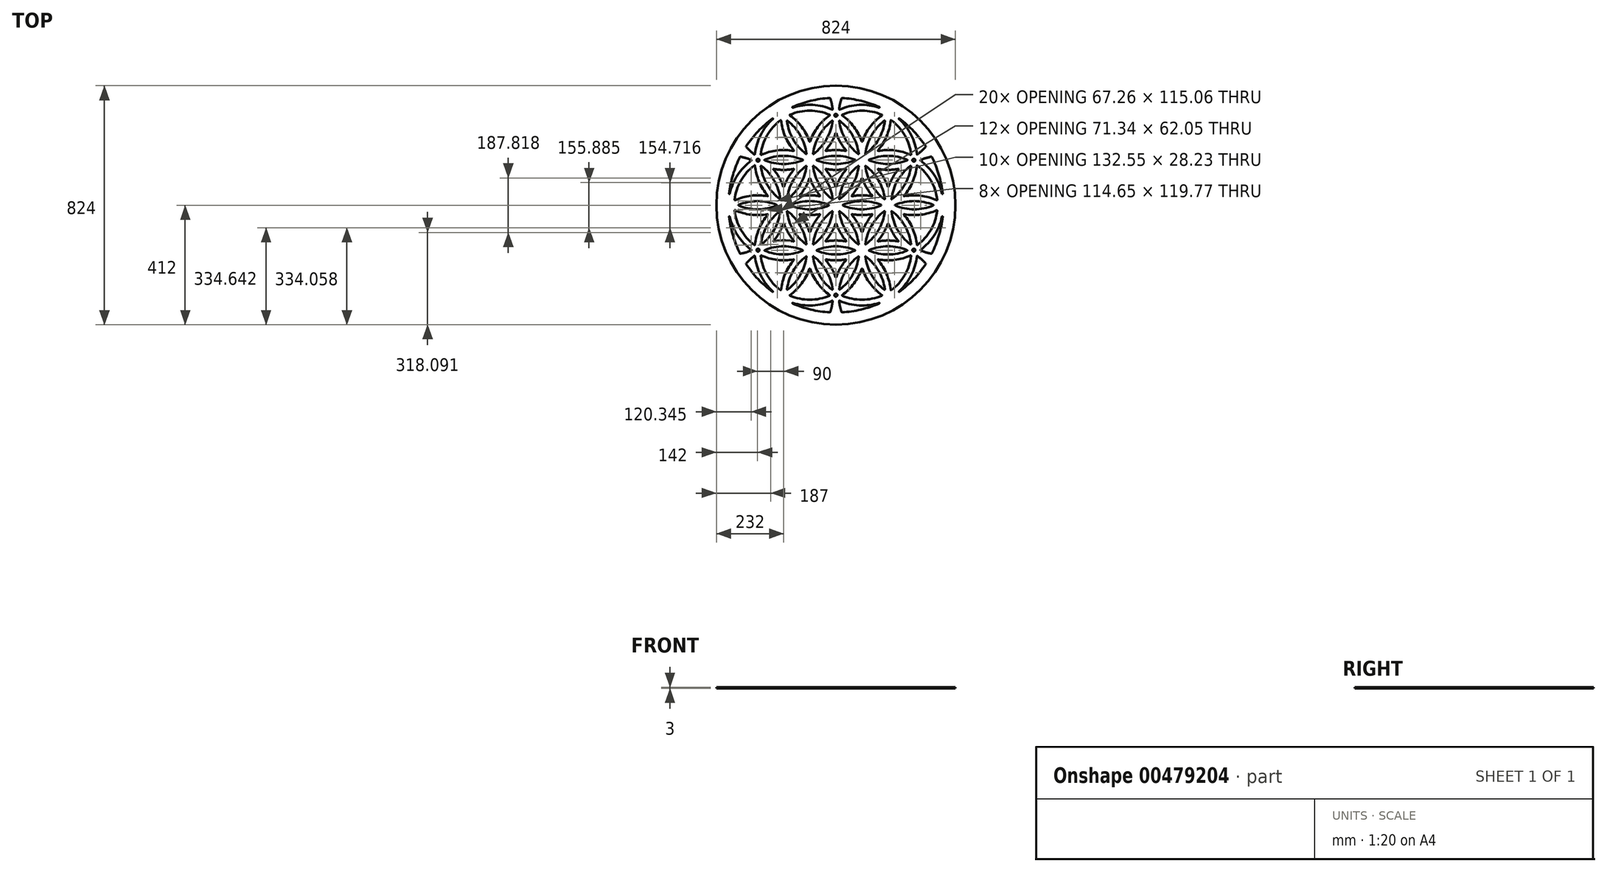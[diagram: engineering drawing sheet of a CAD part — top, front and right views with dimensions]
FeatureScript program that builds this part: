
annotation { "Feature Type Name" : "Feature", "Feature Type Description" : "" }
export const myFeature = defineFeature(function(context is Context, id is Id, definition is map)
    precondition{}
    {
        {
            var Q0;
            Q0=qCreatedBy(makeId("Top.planeOp"),FACE);
            var sketch = newSketch(context, id + "F0", { "sketchPlane" : qUnion([Q0])});
            skArc(sketch, "E0", {"start": v(-280.58, 137.05) * mm, "mid": v(-327.22, 85) * mm, "end": v(-348.98, 18.58) * mm});
            skArc(sketch, "E1", {"start": v(-291.41, 153.9) * mm, "mid": v(-339.34, 103.5) * mm, "end": v(-365.91, 39.2) * mm});
            skArc(sketch, "E2", {"start": v(-190.58, 292.94) * mm, "mid": v(-237.22, 240.88) * mm, "end": v(-258.98, 174.46) * mm});
            skArc(sketch, "E3", {"start": v(-21.41, 309.8) * mm, "mid": v(-62.1, 269.75) * mm, "end": v(-89.06, 219.43) * mm});
            skArc(sketch, "E4", {"start": v(257.58, 173.44) * mm, "mid": v(202.56, 188.66) * mm, "end": v(145.5, 186.84) * mm});
            skArc(sketch, "E5", {"start": v(179.06, 63.55) * mm, "mid": v(164.54, 95) * mm, "end": v(144.56, 123.3) * mm});
            skArc(sketch, "E6", {"start": v(-234.56, -32.6) * mm, "mid": v(-264.66, -81.1) * mm, "end": v(-279, -136.35) * mm});
            skArc(sketch, "E7", {"start": v(-192.97, -20.62) * mm, "mid": v(-237.22, -70.88) * mm, "end": v(-258.63, -134.35) * mm});
            skArc(sketch, "E8", {"start": v(155.66, 0.92) * mm, "mid": v(90, 14.12) * mm, "end": v(24.34, 0.92) * mm});
            skCircle(sketch, "E9", {"center": v(0, 0) * mm, "radius": 412 * mm});
            skArc(sketch, "E10", {"start": v(329.26, 167.2) * mm, "mid": v(310.1, 162.5) * mm, "end": v(291.6, 155.63) * mm});
            skArc(sketch, "E11", {"start": v(309.43, -201.55) * mm, "mid": v(295.78, -187.3) * mm, "end": v(280.58, -174.72) * mm});
            skArc(sketch, "E12", {"start": v(-214.5, 124.93) * mm, "mid": v(-180, 121.77) * mm, "end": v(-145.5, 124.93) * mm});
            skArc(sketch, "E13", {"start": v(-309.43, 201.55) * mm, "mid": v(-295.78, 187.3) * mm, "end": v(-280.58, 174.72) * mm});
            skArc(sketch, "E14", {"start": v(19.83, 368.75) * mm, "mid": v(14.3, 349.8) * mm, "end": v(11.02, 330.35) * mm});
            skArc(sketch, "E15", {"start": v(-20.83, 369.41) * mm, "mid": v(-86.68, 359.7) * mm, "end": v(-149.71, 338.36) * mm});
            skArc(sketch, "E16.trimOffspring", {"start": v(-329.26, -167.2) * mm, "mid": v(-310.1, -162.5) * mm, "end": v(-291.6, -155.63) * mm});
            skArc(sketch, "E17.trimOffspring", {"start": v(-19.83, -368.75) * mm, "mid": v(-14.3, -349.8) * mm, "end": v(-11.02, -330.35) * mm});
            skArc(sketch, "E18.trimOffspring", {"start": v(-189, 292.24) * mm, "mid": v(-174.66, 236.98) * mm, "end": v(-144.56, 188.47) * mm});
            skArc(sketch, "E19.trimOffspring", {"start": v(-12.42, 329.32) * mm, "mid": v(-80.04, 345.62) * mm, "end": v(-149, 336.5) * mm});
            skArc(sketch, "E20.trimOffspring", {"start": v(-11.02, 330.35) * mm, "mid": v(-14.3, 349.8) * mm, "end": v(-19.83, 368.75) * mm});
            skArc(sketch, "E21.trimOffspring", {"start": v(0.94, 248.22) * mm, "mid": v(15.46, 216.77) * mm, "end": v(35.44, 188.47) * mm});
            skArc(sketch, "E22.trimOffspring", {"start": v(-21.6, 311.52) * mm, "mid": v(-90, 325.88) * mm, "end": v(-158.4, 311.52) * mm});
            skArc(sketch, "E23.trimOffspring", {"start": v(11.37, 290.23) * mm, "mid": v(32.78, 226.77) * mm, "end": v(77.03, 176.5) * mm});
            skArc(sketch, "E24.trimOffspring", {"start": v(-12.97, 291.15) * mm, "mid": v(-57.22, 240.88) * mm, "end": v(-78.63, 177.42) * mm});
            skArc(sketch, "E25.trimOffspring", {"start": v(158.59, 309.8) * mm, "mid": v(117.9, 269.75) * mm, "end": v(90.94, 219.43) * mm});
            skArc(sketch, "E26.trimOffspring", {"start": v(167.03, 291.15) * mm, "mid": v(122.78, 240.88) * mm, "end": v(101.37, 177.42) * mm});
            skArc(sketch, "E27.trimOffspring", {"start": v(158.4, 311.52) * mm, "mid": v(90, 325.88) * mm, "end": v(21.6, 311.52) * mm});
            skArc(sketch, "E28.trimOffspring", {"start": v(-279, 136.35) * mm, "mid": v(-264.66, 81.1) * mm, "end": v(-234.56, 32.6) * mm});
            skArc(sketch, "E29.trimOffspring", {"start": v(-291.6, 155.63) * mm, "mid": v(-310.1, 162.5) * mm, "end": v(-329.26, 167.2) * mm});
            skArc(sketch, "E30.trimOffspring", {"start": v(-258.63, 134.35) * mm, "mid": v(-237.22, 70.88) * mm, "end": v(-192.97, 20.62) * mm});
            skArc(sketch, "E31.trimOffspring", {"start": v(-245.66, 154.96) * mm, "mid": v(-180, 141.77) * mm, "end": v(-114.34, 154.96) * mm});
            skArc(sketch, "E32.trimOffspring", {"start": v(280.58, 174.72) * mm, "mid": v(295.78, 187.3) * mm, "end": v(309.43, 201.55) * mm});
            skArc(sketch, "E33.trimOffspring", {"start": v(279, 175.42) * mm, "mid": v(259.3, 242.13) * mm, "end": v(216.91, 297.28) * mm});
            skArc(sketch, "E34.trimOffspring", {"start": v(257.03, 135.27) * mm, "mid": v(212.78, 85) * mm, "end": v(191.37, 21.54) * mm});
            skArc(sketch, "E35.trimOffspring", {"start": v(245.66, 156.8) * mm, "mid": v(180, 170) * mm, "end": v(114.34, 156.8) * mm});
            skArc(sketch, "E36.trimOffspring", {"start": v(215.44, 123.3) * mm, "mid": v(195.46, 95) * mm, "end": v(180.94, 63.55) * mm});
            skArc(sketch, "E37.trimOffspring", {"start": v(258.98, 174.46) * mm, "mid": v(237.22, 240.88) * mm, "end": v(190.58, 292.94) * mm});
            skArc(sketch, "E38.trimOffspring", {"start": v(235.5, -30.96) * mm, "mid": v(292.56, -32.77) * mm, "end": v(347.58, -17.56) * mm});
            skArc(sketch, "E39.trimOffspring", {"start": v(204.34, -0.92) * mm, "mid": v(270, -14.12) * mm, "end": v(335.66, -0.92) * mm});
            skArc(sketch, "E40.trimOffspring", {"start": v(234.56, 32.6) * mm, "mid": v(264.66, 81.1) * mm, "end": v(279, 136.35) * mm});
            skArc(sketch, "E41.trimOffspring", {"start": v(180.94, -63.55) * mm, "mid": v(195.46, -95) * mm, "end": v(215.44, -123.3) * mm});
            skArc(sketch, "E42.trimOffspring", {"start": v(192.97, 20.62) * mm, "mid": v(237.22, 70.88) * mm, "end": v(258.63, 134.35) * mm});
            skArc(sketch, "E43.trimOffspring", {"start": v(124.5, 30.96) * mm, "mid": v(90, 34.12) * mm, "end": v(55.5, 30.96) * mm});
            skArc(sketch, "E44.trimOffspring", {"start": v(125.44, -32.6) * mm, "mid": v(105.46, -60.88) * mm, "end": v(90.94, -92.34) * mm});
            skArc(sketch, "E45.trimOffspring", {"start": v(167.03, -20.62) * mm, "mid": v(122.78, -70.88) * mm, "end": v(101.37, -134.35) * mm});
            skArc(sketch, "E46.trimOffspring", {"start": v(168.63, 21.54) * mm, "mid": v(147.22, 85) * mm, "end": v(102.97, 135.27) * mm});
            skArc(sketch, "E47.trimOffspring", {"start": v(191.37, -21.54) * mm, "mid": v(212.78, -85) * mm, "end": v(257.03, -135.27) * mm});
            skArc(sketch, "E48.trimOffspring", {"start": v(145.5, 124.93) * mm, "mid": v(180, 121.77) * mm, "end": v(214.5, 124.93) * mm});
            skArc(sketch, "E49.trimOffspring", {"start": v(-348.98, -18.58) * mm, "mid": v(-327.22, -85) * mm, "end": v(-280.58, -137.05) * mm});
            skArc(sketch, "E50.trimOffspring", {"start": v(-335.66, -0.92) * mm, "mid": v(-270, -14.12) * mm, "end": v(-204.34, -0.92) * mm});
            skArc(sketch, "E51.trimOffspring", {"start": v(-347.58, -17.56) * mm, "mid": v(-292.56, -32.77) * mm, "end": v(-235.5, -30.96) * mm});
            skArc(sketch, "E52.trimOffspring", {"start": v(-365.91, -39.2) * mm, "mid": v(-339.34, -103.5) * mm, "end": v(-291.41, -153.9) * mm});
            skArc(sketch, "E53.trimOffspring", {"start": v(-145.5, 186.84) * mm, "mid": v(-202.56, 188.66) * mm, "end": v(-257.58, 173.44) * mm});
            skArc(sketch, "E54.trimOffspring", {"start": v(-77.03, 176.5) * mm, "mid": v(-32.78, 226.77) * mm, "end": v(-11.37, 290.23) * mm});
            skArc(sketch, "E55.trimOffspring", {"start": v(-168.63, 290.23) * mm, "mid": v(-147.22, 226.77) * mm, "end": v(-102.97, 176.5) * mm});
            skArc(sketch, "E56.trimOffspring", {"start": v(-34.5, 124.93) * mm, "mid": v(0, 121.77) * mm, "end": v(34.5, 124.93) * mm});
            skArc(sketch, "E57.trimOffspring", {"start": v(-78.63, 134.35) * mm, "mid": v(-57.22, 70.88) * mm, "end": v(-12.97, 20.62) * mm});
            skArc(sketch, "E58.trimOffspring", {"start": v(-89.06, 92.34) * mm, "mid": v(-74.54, 60.88) * mm, "end": v(-54.56, 32.6) * mm});
            skArc(sketch, "E59.trimOffspring", {"start": v(-102.97, 135.27) * mm, "mid": v(-147.22, 85) * mm, "end": v(-168.63, 21.54) * mm});
            skArc(sketch, "E60.trimOffspring", {"start": v(-114.34, 156.8) * mm, "mid": v(-180, 170) * mm, "end": v(-245.66, 156.8) * mm});
            skArc(sketch, "E61.trimOffspring", {"start": v(-144.56, 123.3) * mm, "mid": v(-164.54, 95) * mm, "end": v(-179.06, 63.55) * mm});
            skArc(sketch, "E62.trimOffspring", {"start": v(-180.94, 63.55) * mm, "mid": v(-195.46, 95) * mm, "end": v(-215.44, 123.3) * mm});
            skArc(sketch, "E63.trimOffspring", {"start": v(-35.44, 188.47) * mm, "mid": v(-15.46, 216.77) * mm, "end": v(-0.94, 248.22) * mm});
            skArc(sketch, "E64.trimOffspring", {"start": v(34.5, 186.84) * mm, "mid": v(0, 190) * mm, "end": v(-34.5, 186.84) * mm});
            skArc(sketch, "E65.trimOffspring", {"start": v(-90.94, 219.43) * mm, "mid": v(-117.9, 269.75) * mm, "end": v(-158.59, 309.8) * mm});
            skArc(sketch, "E66.trimOffspring", {"start": v(-101.37, 177.42) * mm, "mid": v(-122.78, 240.88) * mm, "end": v(-167.03, 291.15) * mm});
            skArc(sketch, "E67.trimOffspring", {"start": v(-65.66, 154.96) * mm, "mid": v(0, 141.77) * mm, "end": v(65.66, 154.96) * mm});
            skArc(sketch, "E68.trimOffspring", {"start": v(-216.91, 297.28) * mm, "mid": v(-259.3, 242.13) * mm, "end": v(-279, 175.42) * mm});
            skArc(sketch, "E69.trimOffspring", {"start": v(-218.17, 298.84) * mm, "mid": v(-268.18, 254.92) * mm, "end": v(-309.5, 202.75) * mm});
            skArc(sketch, "E70.trimOffspring", {"start": v(-330.34, 166.67) * mm, "mid": v(-354.85, 104.79) * mm, "end": v(-367.88, 39.52) * mm});
            skArc(sketch, "E71.trimOffspring", {"start": v(149, 336.5) * mm, "mid": v(80.04, 345.62) * mm, "end": v(12.42, 329.32) * mm});
            skArc(sketch, "E72.trimOffspring", {"start": v(149.71, 338.36) * mm, "mid": v(86.68, 359.7) * mm, "end": v(20.83, 369.41) * mm});
            skArc(sketch, "E73.trimOffspring", {"start": v(309.5, 202.75) * mm, "mid": v(268.18, 254.92) * mm, "end": v(218.17, 298.84) * mm});
            skArc(sketch, "E74.trimOffspring", {"start": v(90.94, 92.34) * mm, "mid": v(105.46, 60.88) * mm, "end": v(125.44, 32.6) * mm});
            skArc(sketch, "E75.trimOffspring", {"start": v(35.44, 123.3) * mm, "mid": v(15.46, 95) * mm, "end": v(0.94, 63.55) * mm});
            skArc(sketch, "E76.trimOffspring", {"start": v(89.06, 219.43) * mm, "mid": v(62.1, 269.75) * mm, "end": v(21.41, 309.8) * mm});
            skArc(sketch, "E77.trimOffspring", {"start": v(144.56, 188.47) * mm, "mid": v(174.66, 236.98) * mm, "end": v(189, 292.24) * mm});
            skArc(sketch, "E78.trimOffspring", {"start": v(102.97, 176.5) * mm, "mid": v(147.22, 226.77) * mm, "end": v(168.63, 290.23) * mm});
            skArc(sketch, "E79.trimOffspring", {"start": v(78.63, 177.42) * mm, "mid": v(57.22, 240.88) * mm, "end": v(12.97, 291.15) * mm});
            skArc(sketch, "E80.trimOffspring", {"start": v(114.34, 154.96) * mm, "mid": v(180, 141.77) * mm, "end": v(245.66, 154.96) * mm});
            skArc(sketch, "E81.trimOffspring", {"start": v(101.37, 134.35) * mm, "mid": v(122.78, 70.88) * mm, "end": v(167.03, 20.62) * mm});
            skArc(sketch, "E82.trimOffspring", {"start": v(77.03, 135.27) * mm, "mid": v(32.78, 85) * mm, "end": v(11.37, 21.54) * mm});
            skArc(sketch, "E83.trimOffspring", {"start": v(65.66, 156.8) * mm, "mid": v(0, 170) * mm, "end": v(-65.66, 156.8) * mm});
            skArc(sketch, "E84.trimOffspring", {"start": v(-367.88, -39.52) * mm, "mid": v(-354.85, -104.79) * mm, "end": v(-330.34, -166.67) * mm});
            skArc(sketch, "E85.trimOffspring", {"start": v(-235.5, 30.96) * mm, "mid": v(-292.56, 32.77) * mm, "end": v(-347.58, 17.56) * mm});
            skArc(sketch, "E86.trimOffspring", {"start": v(-124.5, -30.96) * mm, "mid": v(-90, -34.12) * mm, "end": v(-55.5, -30.96) * mm});
            skArc(sketch, "E87.trimOffspring", {"start": v(-179.06, -63.55) * mm, "mid": v(-164.54, -95) * mm, "end": v(-144.56, -123.3) * mm});
            skArc(sketch, "E88.trimOffspring", {"start": v(-125.44, 32.6) * mm, "mid": v(-105.46, 60.88) * mm, "end": v(-90.94, 92.34) * mm});
            skArc(sketch, "E89.trimOffspring", {"start": v(-204.34, 0.92) * mm, "mid": v(-270, 14.12) * mm, "end": v(-335.66, 0.92) * mm});
            skArc(sketch, "E90.trimOffspring", {"start": v(-191.37, 21.54) * mm, "mid": v(-212.78, 85) * mm, "end": v(-257.03, 135.27) * mm});
            skArc(sketch, "E91.trimOffspring", {"start": v(-167.03, 20.62) * mm, "mid": v(-122.78, 70.88) * mm, "end": v(-101.37, 134.35) * mm});
            skArc(sketch, "E92.trimOffspring", {"start": v(-155.66, -0.92) * mm, "mid": v(-90, -14.12) * mm, "end": v(-24.34, -0.92) * mm});
            skArc(sketch, "E93.trimOffspring", {"start": v(-168.63, -21.54) * mm, "mid": v(-147.22, -85) * mm, "end": v(-102.97, -135.27) * mm});
            skArc(sketch, "E94.trimOffspring", {"start": v(335.66, 0.92) * mm, "mid": v(270, 14.12) * mm, "end": v(204.34, 0.92) * mm});
            skArc(sketch, "E95.trimOffspring", {"start": v(347.58, 17.56) * mm, "mid": v(292.56, 32.77) * mm, "end": v(235.5, 30.96) * mm});
            skArc(sketch, "E96.trimOffspring", {"start": v(348.98, 18.58) * mm, "mid": v(327.22, 85) * mm, "end": v(280.58, 137.05) * mm});
            skArc(sketch, "E97.trimOffspring", {"start": v(365.91, 39.2) * mm, "mid": v(339.34, 103.5) * mm, "end": v(291.41, 153.9) * mm});
            skArc(sketch, "E98.trimOffspring", {"start": v(367.88, 39.52) * mm, "mid": v(354.85, 104.79) * mm, "end": v(330.34, 166.67) * mm});
            skArc(sketch, "E99.trimOffspring", {"start": v(-11.37, 21.54) * mm, "mid": v(-32.78, 85) * mm, "end": v(-77.03, 135.27) * mm});
            skArc(sketch, "E100.trimOffspring", {"start": v(-0.94, 63.55) * mm, "mid": v(-15.46, 95) * mm, "end": v(-35.44, 123.3) * mm});
            skArc(sketch, "E101.trimOffspring", {"start": v(12.97, 20.62) * mm, "mid": v(57.22, 70.88) * mm, "end": v(78.63, 134.35) * mm});
            skArc(sketch, "E102.trimOffspring", {"start": v(54.56, 32.6) * mm, "mid": v(74.54, 60.88) * mm, "end": v(89.06, 92.34) * mm});
            skArc(sketch, "E103.trimOffspring", {"start": v(24.34, -0.92) * mm, "mid": v(90, -14.12) * mm, "end": v(155.66, -0.92) * mm});
            skArc(sketch, "E104.trimOffspring", {"start": v(55.5, -30.96) * mm, "mid": v(90, -34.12) * mm, "end": v(124.5, -30.96) * mm});
            skArc(sketch, "E105.trimOffspring", {"start": v(0.94, -63.55) * mm, "mid": v(15.46, -95) * mm, "end": v(35.44, -123.3) * mm});
            skArc(sketch, "E106.trimOffspring", {"start": v(11.37, -21.54) * mm, "mid": v(32.78, -85) * mm, "end": v(77.03, -135.27) * mm});
            skArc(sketch, "E107.trimOffspring", {"start": v(-12.97, -20.62) * mm, "mid": v(-57.22, -70.88) * mm, "end": v(-78.63, -134.35) * mm});
            skArc(sketch, "E108.trimOffspring", {"start": v(-54.56, -32.6) * mm, "mid": v(-74.54, -60.88) * mm, "end": v(-89.06, -92.34) * mm});
            skArc(sketch, "E109.trimOffspring", {"start": v(-24.34, 0.92) * mm, "mid": v(-90, 14.12) * mm, "end": v(-155.66, 0.92) * mm});
            skArc(sketch, "E110.trimOffspring", {"start": v(-55.5, 30.96) * mm, "mid": v(-90, 34.12) * mm, "end": v(-124.5, 30.96) * mm});
            skArc(sketch, "E111.trimOffspring", {"start": v(-309.5, -202.75) * mm, "mid": v(-268.18, -254.92) * mm, "end": v(-218.17, -298.84) * mm});
            skArc(sketch, "E112.trimOffspring", {"start": v(-279, -175.42) * mm, "mid": v(-259.3, -242.13) * mm, "end": v(-216.91, -297.28) * mm});
            skArc(sketch, "E113.trimOffspring", {"start": v(-280.58, -174.72) * mm, "mid": v(-295.78, -187.3) * mm, "end": v(-309.43, -201.55) * mm});
            skArc(sketch, "E114.trimOffspring", {"start": v(-215.44, -123.3) * mm, "mid": v(-195.46, -95) * mm, "end": v(-180.94, -63.55) * mm});
            skArc(sketch, "E115.trimOffspring", {"start": v(-257.03, -135.27) * mm, "mid": v(-212.78, -85) * mm, "end": v(-191.37, -21.54) * mm});
            skArc(sketch, "E116.trimOffspring", {"start": v(-257.58, -173.44) * mm, "mid": v(-202.56, -188.66) * mm, "end": v(-145.5, -186.84) * mm});
            skArc(sketch, "E117.trimOffspring", {"start": v(-258.98, -174.46) * mm, "mid": v(-237.22, -240.88) * mm, "end": v(-190.58, -292.94) * mm});
            skArc(sketch, "E118.trimOffspring", {"start": v(-245.66, -156.8) * mm, "mid": v(-180, -170) * mm, "end": v(-114.34, -156.8) * mm});
            skArc(sketch, "E119.trimOffspring", {"start": v(-167.03, -291.15) * mm, "mid": v(-122.78, -240.88) * mm, "end": v(-101.37, -177.42) * mm});
            skArc(sketch, "E120.trimOffspring", {"start": v(-149, -336.5) * mm, "mid": v(-80.04, -345.62) * mm, "end": v(-12.42, -329.32) * mm});
            skArc(sketch, "E121.trimOffspring", {"start": v(-149.71, -338.36) * mm, "mid": v(-86.68, -359.7) * mm, "end": v(-20.83, -369.41) * mm});
            skArc(sketch, "E122.trimOffspring", {"start": v(-158.59, -309.8) * mm, "mid": v(-117.9, -269.75) * mm, "end": v(-90.94, -219.43) * mm});
            skArc(sketch, "E123.trimOffspring", {"start": v(-158.4, -311.52) * mm, "mid": v(-90, -325.88) * mm, "end": v(-21.6, -311.52) * mm});
            skArc(sketch, "E124.trimOffspring", {"start": v(-114.34, -154.96) * mm, "mid": v(-180, -141.77) * mm, "end": v(-245.66, -154.96) * mm});
            skArc(sketch, "E125.trimOffspring", {"start": v(-145.5, -124.93) * mm, "mid": v(-180, -121.77) * mm, "end": v(-214.5, -124.93) * mm});
            skArc(sketch, "E126.trimOffspring", {"start": v(-101.37, -134.35) * mm, "mid": v(-122.78, -70.88) * mm, "end": v(-167.03, -20.62) * mm});
            skArc(sketch, "E127.trimOffspring", {"start": v(-90.94, -92.34) * mm, "mid": v(-105.46, -60.88) * mm, "end": v(-125.44, -32.6) * mm});
            skArc(sketch, "E128.trimOffspring", {"start": v(-77.03, -135.27) * mm, "mid": v(-32.78, -85) * mm, "end": v(-11.37, -21.54) * mm});
            skArc(sketch, "E129.trimOffspring", {"start": v(-35.44, -123.3) * mm, "mid": v(-15.46, -95) * mm, "end": v(-0.94, -63.55) * mm});
            skArc(sketch, "E130.trimOffspring", {"start": v(-65.66, -156.8) * mm, "mid": v(0, -170) * mm, "end": v(65.66, -156.8) * mm});
            skArc(sketch, "E131.trimOffspring", {"start": v(-34.5, -186.84) * mm, "mid": v(0, -190) * mm, "end": v(34.5, -186.84) * mm});
            skArc(sketch, "E132.trimOffspring", {"start": v(-78.63, -177.42) * mm, "mid": v(-57.22, -240.88) * mm, "end": v(-12.97, -291.15) * mm});
            skArc(sketch, "E133.trimOffspring", {"start": v(-89.06, -219.43) * mm, "mid": v(-62.1, -269.75) * mm, "end": v(-21.41, -309.8) * mm});
            skArc(sketch, "E134.trimOffspring", {"start": v(-102.97, -176.5) * mm, "mid": v(-147.22, -226.77) * mm, "end": v(-168.63, -290.23) * mm});
            skArc(sketch, "E135.trimOffspring", {"start": v(-144.56, -188.47) * mm, "mid": v(-174.66, -236.98) * mm, "end": v(-189, -292.24) * mm});
            skArc(sketch, "E136.trimOffspring", {"start": v(65.66, -154.96) * mm, "mid": v(0, -141.77) * mm, "end": v(-65.66, -154.96) * mm});
            skArc(sketch, "E137.trimOffspring", {"start": v(34.5, -124.93) * mm, "mid": v(0, -121.77) * mm, "end": v(-34.5, -124.93) * mm});
            skArc(sketch, "E138.trimOffspring", {"start": v(78.63, -134.35) * mm, "mid": v(57.22, -70.88) * mm, "end": v(12.97, -20.62) * mm});
            skArc(sketch, "E139.trimOffspring", {"start": v(89.06, -92.34) * mm, "mid": v(74.54, -60.88) * mm, "end": v(54.56, -32.6) * mm});
            skArc(sketch, "E140.trimOffspring", {"start": v(102.97, -135.27) * mm, "mid": v(147.22, -85) * mm, "end": v(168.63, -21.54) * mm});
            skArc(sketch, "E141.trimOffspring", {"start": v(144.56, -123.3) * mm, "mid": v(164.54, -95) * mm, "end": v(179.06, -63.55) * mm});
            skArc(sketch, "E142.trimOffspring", {"start": v(114.34, -156.8) * mm, "mid": v(180, -170) * mm, "end": v(245.66, -156.8) * mm});
            skArc(sketch, "E143.trimOffspring", {"start": v(145.5, -186.84) * mm, "mid": v(202.56, -188.66) * mm, "end": v(257.58, -173.44) * mm});
            skArc(sketch, "E144.trimOffspring", {"start": v(101.37, -177.42) * mm, "mid": v(122.78, -240.88) * mm, "end": v(167.03, -291.15) * mm});
            skArc(sketch, "E145.trimOffspring", {"start": v(90.94, -219.43) * mm, "mid": v(117.9, -269.75) * mm, "end": v(158.59, -309.8) * mm});
            skArc(sketch, "E146.trimOffspring", {"start": v(77.03, -176.5) * mm, "mid": v(32.78, -226.77) * mm, "end": v(11.37, -290.23) * mm});
            skArc(sketch, "E147.trimOffspring", {"start": v(35.44, -188.47) * mm, "mid": v(15.46, -216.77) * mm, "end": v(0.94, -248.22) * mm});
            skArc(sketch, "E148.trimOffspring", {"start": v(214.5, -124.93) * mm, "mid": v(180, -121.77) * mm, "end": v(145.5, -124.93) * mm});
            skArc(sketch, "E149.trimOffspring", {"start": v(280.58, -137.05) * mm, "mid": v(327.22, -85) * mm, "end": v(348.98, -18.58) * mm});
            skArc(sketch, "E150.trimOffspring", {"start": v(279, -136.35) * mm, "mid": v(264.66, -81.1) * mm, "end": v(234.56, -32.6) * mm});
            skArc(sketch, "E151.trimOffspring", {"start": v(258.63, -134.35) * mm, "mid": v(237.22, -70.88) * mm, "end": v(192.97, -20.62) * mm});
            skArc(sketch, "E152.trimOffspring", {"start": v(245.66, -154.96) * mm, "mid": v(180, -141.77) * mm, "end": v(114.34, -154.96) * mm});
            skArc(sketch, "E153.trimOffspring", {"start": v(291.41, -153.9) * mm, "mid": v(339.34, -103.5) * mm, "end": v(365.91, -39.2) * mm});
            skArc(sketch, "E154.trimOffspring", {"start": v(291.6, -155.63) * mm, "mid": v(310.1, -162.5) * mm, "end": v(329.26, -167.2) * mm});
            skArc(sketch, "E155.trimOffspring", {"start": v(330.34, -166.67) * mm, "mid": v(354.85, -104.79) * mm, "end": v(367.88, -39.52) * mm});
            skArc(sketch, "E156.trimOffspring", {"start": v(168.63, -290.23) * mm, "mid": v(147.22, -226.77) * mm, "end": v(102.97, -176.5) * mm});
            skArc(sketch, "E157.trimOffspring", {"start": v(190.58, -292.94) * mm, "mid": v(237.22, -240.88) * mm, "end": v(258.98, -174.46) * mm});
            skArc(sketch, "E158.trimOffspring", {"start": v(189, -292.24) * mm, "mid": v(174.66, -236.98) * mm, "end": v(144.56, -188.47) * mm});
            skArc(sketch, "E159.trimOffspring", {"start": v(218.17, -298.84) * mm, "mid": v(268.18, -254.92) * mm, "end": v(309.5, -202.75) * mm});
            skArc(sketch, "E160.trimOffspring", {"start": v(216.91, -297.28) * mm, "mid": v(259.3, -242.13) * mm, "end": v(279, -175.42) * mm});
            skArc(sketch, "E161.trimOffspring", {"start": v(20.83, -369.41) * mm, "mid": v(86.68, -359.7) * mm, "end": v(149.71, -338.36) * mm});
            skArc(sketch, "E162.trimOffspring", {"start": v(-0.94, -248.22) * mm, "mid": v(-15.46, -216.77) * mm, "end": v(-35.44, -188.47) * mm});
            skArc(sketch, "E163.trimOffspring", {"start": v(12.42, -329.32) * mm, "mid": v(80.04, -345.62) * mm, "end": v(149, -336.5) * mm});
            skArc(sketch, "E164.trimOffspring", {"start": v(21.6, -311.52) * mm, "mid": v(90, -325.88) * mm, "end": v(158.4, -311.52) * mm});
            skArc(sketch, "E165.trimOffspring", {"start": v(21.41, -309.8) * mm, "mid": v(62.1, -269.75) * mm, "end": v(89.06, -219.43) * mm});
            skArc(sketch, "E166.trimOffspring", {"start": v(11.02, -330.35) * mm, "mid": v(14.3, -349.8) * mm, "end": v(19.83, -368.75) * mm});
            skArc(sketch, "E167.trimOffspring", {"start": v(-11.37, -290.23) * mm, "mid": v(-32.78, -226.77) * mm, "end": v(-77.03, -176.5) * mm});
            skArc(sketch, "E168.trimOffspring", {"start": v(12.97, -291.15) * mm, "mid": v(57.22, -240.88) * mm, "end": v(78.63, -177.42) * mm});
            skArc(sketch, "E169.filletArc", {"start": v(149.71, -338.36) * mm, "mid": v(150.24, -337.08) * mm, "end": v(149, -336.5) * mm});
            skPoint(sketch, "E170.visualSharp", {"position": v(20.09, -369.45) * mm});
            skArc(sketch, "E170.filletArc", {"start": v(19.83, -368.75) * mm, "mid": v(20.22, -369.25) * mm, "end": v(20.83, -369.41) * mm});
            skPoint(sketch, "E171.visualSharp", {"position": v(10.84, -328.6) * mm});
            skArc(sketch, "E171.filletArc", {"start": v(12.42, -329.32) * mm, "mid": v(11.42, -329.43) * mm, "end": v(11.02, -330.35) * mm});
            skArc(sketch, "E172.filletArc", {"start": v(216.91, -297.28) * mm, "mid": v(216.8, -298.66) * mm, "end": v(218.17, -298.84) * mm});
            skPoint(sketch, "E173.visualSharp", {"position": v(309.91, -202.12) * mm});
            skArc(sketch, "E173.filletArc", {"start": v(309.5, -202.75) * mm, "mid": v(309.67, -202.14) * mm, "end": v(309.43, -201.55) * mm});
            skPoint(sketch, "E174.visualSharp", {"position": v(279.16, -173.69) * mm});
            skArc(sketch, "E174.filletArc", {"start": v(280.58, -174.72) * mm, "mid": v(279.58, -174.6) * mm, "end": v(279, -175.42) * mm});
            skPoint(sketch, "E175.visualSharp", {"position": v(290, -154.92) * mm});
            skArc(sketch, "E175.filletArc", {"start": v(291.41, -153.9) * mm, "mid": v(291, -154.82) * mm, "end": v(291.6, -155.63) * mm});
            skPoint(sketch, "E176.visualSharp", {"position": v(330, -167.33) * mm});
            skArc(sketch, "E176.filletArc", {"start": v(329.26, -167.2) * mm, "mid": v(329.89, -167.11) * mm, "end": v(330.34, -166.67) * mm});
            skArc(sketch, "E177.filletArc", {"start": v(367.88, -39.52) * mm, "mid": v(367.05, -38.43) * mm, "end": v(365.91, -39.2) * mm});
            skArc(sketch, "E178.filletArc", {"start": v(365.91, 39.2) * mm, "mid": v(367.05, 38.43) * mm, "end": v(367.88, 39.52) * mm});
            skPoint(sketch, "E179.visualSharp", {"position": v(330, 167.33) * mm});
            skArc(sketch, "E179.filletArc", {"start": v(330.34, 166.67) * mm, "mid": v(329.89, 167.11) * mm, "end": v(329.26, 167.2) * mm});
            skPoint(sketch, "E180.visualSharp", {"position": v(290, 154.92) * mm});
            skArc(sketch, "E180.filletArc", {"start": v(291.6, 155.63) * mm, "mid": v(291, 154.82) * mm, "end": v(291.41, 153.9) * mm});
            skPoint(sketch, "E181.visualSharp", {"position": v(279.16, 173.69) * mm});
            skArc(sketch, "E181.filletArc", {"start": v(279, 175.42) * mm, "mid": v(279.58, 174.6) * mm, "end": v(280.58, 174.72) * mm});
            skPoint(sketch, "E182.visualSharp", {"position": v(309.91, 202.12) * mm});
            skArc(sketch, "E182.filletArc", {"start": v(309.43, 201.55) * mm, "mid": v(309.67, 202.14) * mm, "end": v(309.5, 202.75) * mm});
            skArc(sketch, "E183.filletArc", {"start": v(218.17, 298.84) * mm, "mid": v(216.8, 298.66) * mm, "end": v(216.91, 297.28) * mm});
            skArc(sketch, "E184.filletArc", {"start": v(149, 336.5) * mm, "mid": v(150.24, 337.08) * mm, "end": v(149.71, 338.36) * mm});
            skPoint(sketch, "E185.visualSharp", {"position": v(20.09, 369.45) * mm});
            skArc(sketch, "E185.filletArc", {"start": v(20.83, 369.41) * mm, "mid": v(20.22, 369.25) * mm, "end": v(19.83, 368.75) * mm});
            skPoint(sketch, "E186.visualSharp", {"position": v(10.84, 328.6) * mm});
            skArc(sketch, "E186.filletArc", {"start": v(11.02, 330.35) * mm, "mid": v(11.42, 329.43) * mm, "end": v(12.42, 329.32) * mm});
            skPoint(sketch, "E187.visualSharp", {"position": v(-20.09, 369.45) * mm});
            skArc(sketch, "E187.filletArc", {"start": v(-19.83, 368.75) * mm, "mid": v(-20.22, 369.25) * mm, "end": v(-20.83, 369.41) * mm});
            skPoint(sketch, "E188.visualSharp", {"position": v(-10.84, 328.6) * mm});
            skArc(sketch, "E188.filletArc", {"start": v(-12.42, 329.32) * mm, "mid": v(-11.42, 329.43) * mm, "end": v(-11.02, 330.35) * mm});
            skArc(sketch, "E189.filletArc", {"start": v(-149.71, 338.36) * mm, "mid": v(-150.24, 337.08) * mm, "end": v(-149, 336.5) * mm});
            skArc(sketch, "E190.filletArc", {"start": v(-216.91, 297.28) * mm, "mid": v(-216.8, 298.66) * mm, "end": v(-218.17, 298.84) * mm});
            skPoint(sketch, "E191.visualSharp", {"position": v(-309.91, 202.12) * mm});
            skArc(sketch, "E191.filletArc", {"start": v(-309.5, 202.75) * mm, "mid": v(-309.67, 202.14) * mm, "end": v(-309.43, 201.55) * mm});
            skPoint(sketch, "E192.visualSharp", {"position": v(-279.16, 173.69) * mm});
            skArc(sketch, "E192.filletArc", {"start": v(-280.58, 174.72) * mm, "mid": v(-279.58, 174.6) * mm, "end": v(-279, 175.42) * mm});
            skPoint(sketch, "E193.visualSharp", {"position": v(-290, 154.92) * mm});
            skArc(sketch, "E193.filletArc", {"start": v(-291.41, 153.9) * mm, "mid": v(-291, 154.82) * mm, "end": v(-291.6, 155.63) * mm});
            skPoint(sketch, "E194.visualSharp", {"position": v(-330, 167.33) * mm});
            skArc(sketch, "E194.filletArc", {"start": v(-329.26, 167.2) * mm, "mid": v(-329.89, 167.11) * mm, "end": v(-330.34, 166.67) * mm});
            skArc(sketch, "E195.filletArc", {"start": v(-367.88, 39.52) * mm, "mid": v(-367.05, 38.43) * mm, "end": v(-365.91, 39.2) * mm});
            skArc(sketch, "E196.filletArc", {"start": v(-365.91, -39.2) * mm, "mid": v(-367.05, -38.43) * mm, "end": v(-367.88, -39.52) * mm});
            skPoint(sketch, "E197.visualSharp", {"position": v(-290, -154.92) * mm});
            skArc(sketch, "E197.filletArc", {"start": v(-291.6, -155.63) * mm, "mid": v(-291, -154.82) * mm, "end": v(-291.41, -153.9) * mm});
            skPoint(sketch, "E198.visualSharp", {"position": v(-330, -167.33) * mm});
            skArc(sketch, "E198.filletArc", {"start": v(-330.34, -166.67) * mm, "mid": v(-329.89, -167.11) * mm, "end": v(-329.26, -167.2) * mm});
            skPoint(sketch, "E199.visualSharp", {"position": v(-279.16, -173.69) * mm});
            skArc(sketch, "E199.filletArc", {"start": v(-279, -175.42) * mm, "mid": v(-279.58, -174.6) * mm, "end": v(-280.58, -174.72) * mm});
            skPoint(sketch, "E200.visualSharp", {"position": v(-309.91, -202.12) * mm});
            skArc(sketch, "E200.filletArc", {"start": v(-309.43, -201.55) * mm, "mid": v(-309.67, -202.14) * mm, "end": v(-309.5, -202.75) * mm});
            skArc(sketch, "E201.filletArc", {"start": v(-218.17, -298.84) * mm, "mid": v(-216.8, -298.66) * mm, "end": v(-216.91, -297.28) * mm});
            skArc(sketch, "E202.filletArc", {"start": v(-149, -336.5) * mm, "mid": v(-150.24, -337.08) * mm, "end": v(-149.71, -338.36) * mm});
            skPoint(sketch, "E203.visualSharp", {"position": v(-20.09, -369.45) * mm});
            skArc(sketch, "E203.filletArc", {"start": v(-20.83, -369.41) * mm, "mid": v(-20.22, -369.25) * mm, "end": v(-19.83, -368.75) * mm});
            skPoint(sketch, "E204.visualSharp", {"position": v(-10.84, -328.6) * mm});
            skArc(sketch, "E204.filletArc", {"start": v(-11.02, -330.35) * mm, "mid": v(-11.42, -329.43) * mm, "end": v(-12.42, -329.32) * mm});
            skPoint(sketch, "E205.visualSharp", {"position": v(20, -310.8) * mm});
            skArc(sketch, "E205.filletArc", {"start": v(21.41, -309.8) * mm, "mid": v(21, -310.7) * mm, "end": v(21.6, -311.52) * mm});
            skPoint(sketch, "E206.visualSharp", {"position": v(160, -310.8) * mm});
            skArc(sketch, "E206.filletArc", {"start": v(158.4, -311.52) * mm, "mid": v(159, -310.7) * mm, "end": v(158.59, -309.8) * mm});
            skPoint(sketch, "E207.visualSharp", {"position": v(90, -216.71) * mm});
            skArc(sketch, "E207.filletArc", {"start": v(90.94, -219.43) * mm, "mid": v(90, -218.77) * mm, "end": v(89.06, -219.43) * mm});
            skPoint(sketch, "E208.visualSharp", {"position": v(11.09, -292.56) * mm});
            skArc(sketch, "E208.filletArc", {"start": v(11.37, -290.23) * mm, "mid": v(11.86, -291.22) * mm, "end": v(12.97, -291.15) * mm});
            skPoint(sketch, "E209.visualSharp", {"position": v(78.91, -175.1) * mm});
            skArc(sketch, "E209.filletArc", {"start": v(78.63, -177.42) * mm, "mid": v(78.14, -176.43) * mm, "end": v(77.03, -176.5) * mm});
            skPoint(sketch, "E210.visualSharp", {"position": v(101.09, -175.1) * mm});
            skArc(sketch, "E210.filletArc", {"start": v(102.97, -176.5) * mm, "mid": v(101.86, -176.43) * mm, "end": v(101.37, -177.42) * mm});
            skPoint(sketch, "E211.visualSharp", {"position": v(168.91, -292.56) * mm});
            skArc(sketch, "E211.filletArc", {"start": v(167.03, -291.15) * mm, "mid": v(168.14, -291.22) * mm, "end": v(168.63, -290.23) * mm});
            skPoint(sketch, "E212.visualSharp", {"position": v(0, -250.94) * mm});
            skArc(sketch, "E212.filletArc", {"start": v(-0.94, -248.22) * mm, "mid": v(0, -248.89) * mm, "end": v(0.94, -248.22) * mm});
            skPoint(sketch, "E213.visualSharp", {"position": v(-37.32, -186.3) * mm});
            skArc(sketch, "E213.filletArc", {"start": v(-34.5, -186.84) * mm, "mid": v(-35.54, -187.33) * mm, "end": v(-35.44, -188.47) * mm});
            skPoint(sketch, "E214.visualSharp", {"position": v(37.32, -186.3) * mm});
            skArc(sketch, "E214.filletArc", {"start": v(35.44, -188.47) * mm, "mid": v(35.54, -187.33) * mm, "end": v(34.5, -186.84) * mm});
            skPoint(sketch, "E215.visualSharp", {"position": v(-11.09, -292.56) * mm});
            skArc(sketch, "E215.filletArc", {"start": v(-12.97, -291.15) * mm, "mid": v(-11.86, -291.22) * mm, "end": v(-11.37, -290.23) * mm});
            skPoint(sketch, "E216.visualSharp", {"position": v(-78.91, -175.1) * mm});
            skArc(sketch, "E216.filletArc", {"start": v(-77.03, -176.5) * mm, "mid": v(-78.14, -176.43) * mm, "end": v(-78.63, -177.42) * mm});
            skPoint(sketch, "E217.visualSharp", {"position": v(-20, -310.8) * mm});
            skArc(sketch, "E217.filletArc", {"start": v(-21.6, -311.52) * mm, "mid": v(-21, -310.7) * mm, "end": v(-21.41, -309.8) * mm});
            skPoint(sketch, "E218.visualSharp", {"position": v(-160, -310.8) * mm});
            skArc(sketch, "E218.filletArc", {"start": v(-158.59, -309.8) * mm, "mid": v(-159, -310.7) * mm, "end": v(-158.4, -311.52) * mm});
            skPoint(sketch, "E219.visualSharp", {"position": v(-90, -216.71) * mm});
            skArc(sketch, "E219.filletArc", {"start": v(-89.06, -219.43) * mm, "mid": v(-90, -218.77) * mm, "end": v(-90.94, -219.43) * mm});
            skPoint(sketch, "E220.visualSharp", {"position": v(-168.91, -292.56) * mm});
            skArc(sketch, "E220.filletArc", {"start": v(-168.63, -290.23) * mm, "mid": v(-168.14, -291.22) * mm, "end": v(-167.03, -291.15) * mm});
            skPoint(sketch, "E221.visualSharp", {"position": v(-101.09, -175.1) * mm});
            skArc(sketch, "E221.filletArc", {"start": v(-101.37, -177.42) * mm, "mid": v(-101.86, -176.43) * mm, "end": v(-102.97, -176.5) * mm});
            skPoint(sketch, "E222.visualSharp", {"position": v(-189.16, -293.97) * mm});
            skArc(sketch, "E222.filletArc", {"start": v(-190.58, -292.94) * mm, "mid": v(-189.58, -293.05) * mm, "end": v(-189, -292.24) * mm});
            skPoint(sketch, "E223.visualSharp", {"position": v(-259.16, -172.72) * mm});
            skArc(sketch, "E223.filletArc", {"start": v(-257.58, -173.44) * mm, "mid": v(-258.58, -173.54) * mm, "end": v(-258.98, -174.46) * mm});
            skPoint(sketch, "E224.visualSharp", {"position": v(-142.68, -186.3) * mm});
            skArc(sketch, "E224.filletArc", {"start": v(-144.56, -188.47) * mm, "mid": v(-144.46, -187.33) * mm, "end": v(-145.5, -186.84) * mm});
            skPoint(sketch, "E225.visualSharp", {"position": v(142.68, -186.3) * mm});
            skArc(sketch, "E225.filletArc", {"start": v(145.5, -186.84) * mm, "mid": v(144.46, -187.33) * mm, "end": v(144.56, -188.47) * mm});
            skPoint(sketch, "E226.visualSharp", {"position": v(189.16, -293.97) * mm});
            skArc(sketch, "E226.filletArc", {"start": v(189, -292.24) * mm, "mid": v(189.58, -293.05) * mm, "end": v(190.58, -292.94) * mm});
            skPoint(sketch, "E227.visualSharp", {"position": v(259.16, -172.72) * mm});
            skArc(sketch, "E227.filletArc", {"start": v(258.98, -174.46) * mm, "mid": v(258.58, -173.54) * mm, "end": v(257.58, -173.44) * mm});
            skPoint(sketch, "E228.visualSharp", {"position": v(-247.82, -155.88) * mm});
            skArc(sketch, "E228.filletArc", {"start": v(-245.66, -154.96) * mm, "mid": v(-246.28, -155.88) * mm, "end": v(-245.66, -156.8) * mm});
            skPoint(sketch, "E229.visualSharp", {"position": v(-112.18, -155.88) * mm});
            skArc(sketch, "E229.filletArc", {"start": v(-114.34, -156.8) * mm, "mid": v(-113.72, -155.88) * mm, "end": v(-114.34, -154.96) * mm});
            skPoint(sketch, "E230.visualSharp", {"position": v(-67.82, -155.88) * mm});
            skArc(sketch, "E230.filletArc", {"start": v(-65.66, -154.96) * mm, "mid": v(-66.28, -155.88) * mm, "end": v(-65.66, -156.8) * mm});
            skPoint(sketch, "E231.visualSharp", {"position": v(67.82, -155.88) * mm});
            skArc(sketch, "E231.filletArc", {"start": v(65.66, -156.8) * mm, "mid": v(66.28, -155.88) * mm, "end": v(65.66, -154.96) * mm});
            skPoint(sketch, "E232.visualSharp", {"position": v(112.18, -155.88) * mm});
            skArc(sketch, "E232.filletArc", {"start": v(114.34, -154.96) * mm, "mid": v(113.72, -155.88) * mm, "end": v(114.34, -156.8) * mm});
            skPoint(sketch, "E233.visualSharp", {"position": v(247.82, -155.88) * mm});
            skArc(sketch, "E233.filletArc", {"start": v(245.66, -156.8) * mm, "mid": v(246.28, -155.88) * mm, "end": v(245.66, -154.96) * mm});
            skPoint(sketch, "E234.visualSharp", {"position": v(191.09, -19.2) * mm});
            skArc(sketch, "E234.filletArc", {"start": v(192.97, -20.62) * mm, "mid": v(191.86, -20.55) * mm, "end": v(191.37, -21.54) * mm});
            skPoint(sketch, "E235.visualSharp", {"position": v(258.91, -136.68) * mm});
            skArc(sketch, "E235.filletArc", {"start": v(257.03, -135.27) * mm, "mid": v(258.14, -135.34) * mm, "end": v(258.63, -134.35) * mm});
            skPoint(sketch, "E236.visualSharp", {"position": v(217.32, -125.47) * mm});
            skArc(sketch, "E236.filletArc", {"start": v(214.5, -124.93) * mm, "mid": v(215.54, -124.44) * mm, "end": v(215.44, -123.3) * mm});
            skPoint(sketch, "E237.visualSharp", {"position": v(180, -60.83) * mm});
            skArc(sketch, "E237.filletArc", {"start": v(180.94, -63.55) * mm, "mid": v(180, -62.88) * mm, "end": v(179.06, -63.55) * mm});
            skPoint(sketch, "E238.visualSharp", {"position": v(142.68, -125.47) * mm});
            skArc(sketch, "E238.filletArc", {"start": v(144.56, -123.3) * mm, "mid": v(144.46, -124.44) * mm, "end": v(145.5, -124.93) * mm});
            skPoint(sketch, "E239.visualSharp", {"position": v(168.91, -19.2) * mm});
            skArc(sketch, "E239.filletArc", {"start": v(168.63, -21.54) * mm, "mid": v(168.14, -20.55) * mm, "end": v(167.03, -20.62) * mm});
            skPoint(sketch, "E240.visualSharp", {"position": v(101.09, -136.68) * mm});
            skArc(sketch, "E240.filletArc", {"start": v(101.37, -134.35) * mm, "mid": v(101.86, -135.34) * mm, "end": v(102.97, -135.27) * mm});
            skPoint(sketch, "E241.visualSharp", {"position": v(90, -95.06) * mm});
            skArc(sketch, "E241.filletArc", {"start": v(89.06, -92.34) * mm, "mid": v(90, -93) * mm, "end": v(90.94, -92.34) * mm});
            skPoint(sketch, "E242.visualSharp", {"position": v(52.68, -30.41) * mm});
            skArc(sketch, "E242.filletArc", {"start": v(55.5, -30.96) * mm, "mid": v(54.46, -31.44) * mm, "end": v(54.56, -32.6) * mm});
            skPoint(sketch, "E243.visualSharp", {"position": v(127.32, -30.41) * mm});
            skArc(sketch, "E243.filletArc", {"start": v(125.44, -32.6) * mm, "mid": v(125.54, -31.44) * mm, "end": v(124.5, -30.96) * mm});
            skPoint(sketch, "E244.visualSharp", {"position": v(11.09, -19.2) * mm});
            skArc(sketch, "E244.filletArc", {"start": v(12.97, -20.62) * mm, "mid": v(11.86, -20.55) * mm, "end": v(11.37, -21.54) * mm});
            skPoint(sketch, "E245.visualSharp", {"position": v(78.91, -136.68) * mm});
            skArc(sketch, "E245.filletArc", {"start": v(77.03, -135.27) * mm, "mid": v(78.14, -135.34) * mm, "end": v(78.63, -134.35) * mm});
            skPoint(sketch, "E246.visualSharp", {"position": v(37.32, -125.47) * mm});
            skArc(sketch, "E246.filletArc", {"start": v(34.5, -124.93) * mm, "mid": v(35.54, -124.44) * mm, "end": v(35.44, -123.3) * mm});
            skPoint(sketch, "E247.visualSharp", {"position": v(-37.32, -125.47) * mm});
            skArc(sketch, "E247.filletArc", {"start": v(-35.44, -123.3) * mm, "mid": v(-35.54, -124.44) * mm, "end": v(-34.5, -124.93) * mm});
            skPoint(sketch, "E248.visualSharp", {"position": v(0, -60.83) * mm});
            skArc(sketch, "E248.filletArc", {"start": v(0.94, -63.55) * mm, "mid": v(0, -62.88) * mm, "end": v(-0.94, -63.55) * mm});
            skPoint(sketch, "E249.visualSharp", {"position": v(279.16, -138.08) * mm});
            skArc(sketch, "E249.filletArc", {"start": v(279, -136.35) * mm, "mid": v(279.58, -137.16) * mm, "end": v(280.58, -137.05) * mm});
            skPoint(sketch, "E250.visualSharp", {"position": v(232.68, -30.41) * mm});
            skArc(sketch, "E250.filletArc", {"start": v(235.5, -30.96) * mm, "mid": v(234.46, -31.44) * mm, "end": v(234.56, -32.6) * mm});
            skPoint(sketch, "E251.visualSharp", {"position": v(349.16, -16.84) * mm});
            skArc(sketch, "E251.filletArc", {"start": v(348.98, -18.58) * mm, "mid": v(348.58, -17.66) * mm, "end": v(347.58, -17.56) * mm});
            skPoint(sketch, "E252.visualSharp", {"position": v(-11.09, -19.2) * mm});
            skArc(sketch, "E252.filletArc", {"start": v(-11.37, -21.54) * mm, "mid": v(-11.86, -20.55) * mm, "end": v(-12.97, -20.62) * mm});
            skPoint(sketch, "E253.visualSharp", {"position": v(-78.91, -136.68) * mm});
            skArc(sketch, "E253.filletArc", {"start": v(-78.63, -134.35) * mm, "mid": v(-78.14, -135.34) * mm, "end": v(-77.03, -135.27) * mm});
            skPoint(sketch, "E254.visualSharp", {"position": v(-90, -95.06) * mm});
            skArc(sketch, "E254.filletArc", {"start": v(-90.94, -92.34) * mm, "mid": v(-90, -93) * mm, "end": v(-89.06, -92.34) * mm});
            skPoint(sketch, "E255.visualSharp", {"position": v(-52.68, -30.41) * mm});
            skArc(sketch, "E255.filletArc", {"start": v(-54.56, -32.6) * mm, "mid": v(-54.46, -31.44) * mm, "end": v(-55.5, -30.96) * mm});
            skPoint(sketch, "E256.visualSharp", {"position": v(-127.32, -30.41) * mm});
            skArc(sketch, "E256.filletArc", {"start": v(-124.5, -30.96) * mm, "mid": v(-125.54, -31.44) * mm, "end": v(-125.44, -32.6) * mm});
            skPoint(sketch, "E257.visualSharp", {"position": v(-168.91, -19.2) * mm});
            skArc(sketch, "E257.filletArc", {"start": v(-167.03, -20.62) * mm, "mid": v(-168.14, -20.55) * mm, "end": v(-168.63, -21.54) * mm});
            skPoint(sketch, "E258.visualSharp", {"position": v(-101.09, -136.68) * mm});
            skArc(sketch, "E258.filletArc", {"start": v(-102.97, -135.27) * mm, "mid": v(-101.86, -135.34) * mm, "end": v(-101.37, -134.35) * mm});
            skPoint(sketch, "E259.visualSharp", {"position": v(-217.32, -125.47) * mm});
            skArc(sketch, "E259.filletArc", {"start": v(-215.44, -123.3) * mm, "mid": v(-215.54, -124.44) * mm, "end": v(-214.5, -124.93) * mm});
            skPoint(sketch, "E260.visualSharp", {"position": v(-180, -60.83) * mm});
            skArc(sketch, "E260.filletArc", {"start": v(-179.06, -63.55) * mm, "mid": v(-180, -62.88) * mm, "end": v(-180.94, -63.55) * mm});
            skPoint(sketch, "E261.visualSharp", {"position": v(-142.68, -125.47) * mm});
            skArc(sketch, "E261.filletArc", {"start": v(-145.5, -124.93) * mm, "mid": v(-144.46, -124.44) * mm, "end": v(-144.56, -123.3) * mm});
            skPoint(sketch, "E262.visualSharp", {"position": v(-258.91, -136.68) * mm});
            skArc(sketch, "E262.filletArc", {"start": v(-258.63, -134.35) * mm, "mid": v(-258.14, -135.34) * mm, "end": v(-257.03, -135.27) * mm});
            skPoint(sketch, "E263.visualSharp", {"position": v(-191.09, -19.2) * mm});
            skArc(sketch, "E263.filletArc", {"start": v(-191.37, -21.54) * mm, "mid": v(-191.86, -20.55) * mm, "end": v(-192.97, -20.62) * mm});
            skPoint(sketch, "E264.visualSharp", {"position": v(-232.68, -30.41) * mm});
            skArc(sketch, "E264.filletArc", {"start": v(-234.56, -32.6) * mm, "mid": v(-234.46, -31.44) * mm, "end": v(-235.5, -30.96) * mm});
            skPoint(sketch, "E265.visualSharp", {"position": v(-349.16, -16.84) * mm});
            skArc(sketch, "E265.filletArc", {"start": v(-347.58, -17.56) * mm, "mid": v(-348.58, -17.66) * mm, "end": v(-348.98, -18.58) * mm});
            skPoint(sketch, "E266.visualSharp", {"position": v(-279.16, -138.08) * mm});
            skArc(sketch, "E266.filletArc", {"start": v(-280.58, -137.05) * mm, "mid": v(-279.58, -137.16) * mm, "end": v(-279, -136.35) * mm});
            skPoint(sketch, "E267.visualSharp", {"position": v(-337.82, 0) * mm});
            skArc(sketch, "E267.filletArc", {"start": v(-335.66, 0.92) * mm, "mid": v(-336.28, 0) * mm, "end": v(-335.66, -0.92) * mm});
            skPoint(sketch, "E268.visualSharp", {"position": v(-202.18, 0) * mm});
            skArc(sketch, "E268.filletArc", {"start": v(-204.34, -0.92) * mm, "mid": v(-203.72, 0) * mm, "end": v(-204.34, 0.92) * mm});
            skPoint(sketch, "E269.visualSharp", {"position": v(-157.82, 0) * mm});
            skArc(sketch, "E269.filletArc", {"start": v(-155.66, 0.92) * mm, "mid": v(-156.28, 0) * mm, "end": v(-155.66, -0.92) * mm});
            skPoint(sketch, "E270.visualSharp", {"position": v(-22.18, 0) * mm});
            skArc(sketch, "E270.filletArc", {"start": v(-24.34, -0.92) * mm, "mid": v(-23.72, 0) * mm, "end": v(-24.34, 0.92) * mm});
            skPoint(sketch, "E271.visualSharp", {"position": v(22.18, 0) * mm});
            skArc(sketch, "E271.filletArc", {"start": v(24.34, 0.92) * mm, "mid": v(23.72, 0) * mm, "end": v(24.34, -0.92) * mm});
            skPoint(sketch, "E272.visualSharp", {"position": v(157.82, 0) * mm});
            skArc(sketch, "E272.filletArc", {"start": v(155.66, -0.92) * mm, "mid": v(156.28, 0) * mm, "end": v(155.66, 0.92) * mm});
            skPoint(sketch, "E273.visualSharp", {"position": v(202.18, 0) * mm});
            skArc(sketch, "E273.filletArc", {"start": v(204.34, 0.92) * mm, "mid": v(203.72, 0) * mm, "end": v(204.34, -0.92) * mm});
            skPoint(sketch, "E274.visualSharp", {"position": v(337.82, 0) * mm});
            skArc(sketch, "E274.filletArc", {"start": v(335.66, -0.92) * mm, "mid": v(336.28, 0) * mm, "end": v(335.66, 0.92) * mm});
            skPoint(sketch, "E275.visualSharp", {"position": v(-349.16, 16.84) * mm});
            skArc(sketch, "E275.filletArc", {"start": v(-348.98, 18.58) * mm, "mid": v(-348.58, 17.66) * mm, "end": v(-347.58, 17.56) * mm});
            skPoint(sketch, "E276.visualSharp", {"position": v(-232.68, 30.41) * mm});
            skArc(sketch, "E276.filletArc", {"start": v(-235.5, 30.96) * mm, "mid": v(-234.46, 31.44) * mm, "end": v(-234.56, 32.6) * mm});
            skPoint(sketch, "E277.visualSharp", {"position": v(-279.16, 138.08) * mm});
            skArc(sketch, "E277.filletArc", {"start": v(-279, 136.35) * mm, "mid": v(-279.58, 137.16) * mm, "end": v(-280.58, 137.05) * mm});
            skPoint(sketch, "E278.visualSharp", {"position": v(-258.91, 136.68) * mm});
            skArc(sketch, "E278.filletArc", {"start": v(-257.03, 135.27) * mm, "mid": v(-258.14, 135.34) * mm, "end": v(-258.63, 134.35) * mm});
            skPoint(sketch, "E279.visualSharp", {"position": v(-191.09, 19.2) * mm});
            skArc(sketch, "E279.filletArc", {"start": v(-192.97, 20.62) * mm, "mid": v(-191.86, 20.55) * mm, "end": v(-191.37, 21.54) * mm});
            skPoint(sketch, "E280.visualSharp", {"position": v(-217.32, 125.47) * mm});
            skArc(sketch, "E280.filletArc", {"start": v(-214.5, 124.93) * mm, "mid": v(-215.54, 124.44) * mm, "end": v(-215.44, 123.3) * mm});
            skPoint(sketch, "E281.visualSharp", {"position": v(-142.68, 125.47) * mm});
            skArc(sketch, "E281.filletArc", {"start": v(-144.56, 123.3) * mm, "mid": v(-144.46, 124.44) * mm, "end": v(-145.5, 124.93) * mm});
            skPoint(sketch, "E282.visualSharp", {"position": v(-180, 60.83) * mm});
            skArc(sketch, "E282.filletArc", {"start": v(-180.94, 63.55) * mm, "mid": v(-180, 62.88) * mm, "end": v(-179.06, 63.55) * mm});
            skPoint(sketch, "E283.visualSharp", {"position": v(-168.91, 19.2) * mm});
            skArc(sketch, "E283.filletArc", {"start": v(-168.63, 21.54) * mm, "mid": v(-168.14, 20.55) * mm, "end": v(-167.03, 20.62) * mm});
            skPoint(sketch, "E284.visualSharp", {"position": v(-101.09, 136.68) * mm});
            skArc(sketch, "E284.filletArc", {"start": v(-101.37, 134.35) * mm, "mid": v(-101.86, 135.34) * mm, "end": v(-102.97, 135.27) * mm});
            skPoint(sketch, "E285.visualSharp", {"position": v(-127.32, 30.41) * mm});
            skArc(sketch, "E285.filletArc", {"start": v(-125.44, 32.6) * mm, "mid": v(-125.54, 31.44) * mm, "end": v(-124.5, 30.96) * mm});
            skPoint(sketch, "E286.visualSharp", {"position": v(-90, 95.06) * mm});
            skArc(sketch, "E286.filletArc", {"start": v(-89.06, 92.34) * mm, "mid": v(-90, 93) * mm, "end": v(-90.94, 92.34) * mm});
            skPoint(sketch, "E287.visualSharp", {"position": v(-52.68, 30.41) * mm});
            skArc(sketch, "E287.filletArc", {"start": v(-55.5, 30.96) * mm, "mid": v(-54.46, 31.44) * mm, "end": v(-54.56, 32.6) * mm});
            skPoint(sketch, "E288.visualSharp", {"position": v(-11.09, 19.2) * mm});
            skArc(sketch, "E288.filletArc", {"start": v(-12.97, 20.62) * mm, "mid": v(-11.86, 20.55) * mm, "end": v(-11.37, 21.54) * mm});
            skPoint(sketch, "E289.visualSharp", {"position": v(-78.91, 136.68) * mm});
            skArc(sketch, "E289.filletArc", {"start": v(-77.03, 135.27) * mm, "mid": v(-78.14, 135.34) * mm, "end": v(-78.63, 134.35) * mm});
            skPoint(sketch, "E290.visualSharp", {"position": v(-37.32, 125.47) * mm});
            skArc(sketch, "E290.filletArc", {"start": v(-34.5, 124.93) * mm, "mid": v(-35.54, 124.44) * mm, "end": v(-35.44, 123.3) * mm});
            skPoint(sketch, "E291.visualSharp", {"position": v(37.32, 125.47) * mm});
            skArc(sketch, "E291.filletArc", {"start": v(35.44, 123.3) * mm, "mid": v(35.54, 124.44) * mm, "end": v(34.5, 124.93) * mm});
            skPoint(sketch, "E292.visualSharp", {"position": v(0, 60.83) * mm});
            skArc(sketch, "E292.filletArc", {"start": v(-0.94, 63.55) * mm, "mid": v(0, 62.88) * mm, "end": v(0.94, 63.55) * mm});
            skPoint(sketch, "E293.visualSharp", {"position": v(78.91, 136.68) * mm});
            skArc(sketch, "E293.filletArc", {"start": v(78.63, 134.35) * mm, "mid": v(78.14, 135.34) * mm, "end": v(77.03, 135.27) * mm});
            skPoint(sketch, "E294.visualSharp", {"position": v(11.09, 19.2) * mm});
            skArc(sketch, "E294.filletArc", {"start": v(11.37, 21.54) * mm, "mid": v(11.86, 20.55) * mm, "end": v(12.97, 20.62) * mm});
            skPoint(sketch, "E295.visualSharp", {"position": v(52.68, 30.41) * mm});
            skArc(sketch, "E295.filletArc", {"start": v(54.56, 32.6) * mm, "mid": v(54.46, 31.44) * mm, "end": v(55.5, 30.96) * mm});
            skPoint(sketch, "E296.visualSharp", {"position": v(127.32, 30.41) * mm});
            skArc(sketch, "E296.filletArc", {"start": v(124.5, 30.96) * mm, "mid": v(125.54, 31.44) * mm, "end": v(125.44, 32.6) * mm});
            skPoint(sketch, "E297.visualSharp", {"position": v(90, 95.06) * mm});
            skArc(sketch, "E297.filletArc", {"start": v(90.94, 92.34) * mm, "mid": v(90, 93) * mm, "end": v(89.06, 92.34) * mm});
            skPoint(sketch, "E298.visualSharp", {"position": v(101.09, 136.68) * mm});
            skArc(sketch, "E298.filletArc", {"start": v(102.97, 135.27) * mm, "mid": v(101.86, 135.34) * mm, "end": v(101.37, 134.35) * mm});
            skPoint(sketch, "E299.visualSharp", {"position": v(168.91, 19.2) * mm});
            skArc(sketch, "E299.filletArc", {"start": v(167.03, 20.62) * mm, "mid": v(168.14, 20.55) * mm, "end": v(168.63, 21.54) * mm});
            skPoint(sketch, "E300.visualSharp", {"position": v(180, 60.83) * mm});
            skArc(sketch, "E300.filletArc", {"start": v(179.06, 63.55) * mm, "mid": v(180, 62.88) * mm, "end": v(180.94, 63.55) * mm});
            skPoint(sketch, "E301.visualSharp", {"position": v(142.68, 125.47) * mm});
            skArc(sketch, "E301.filletArc", {"start": v(145.5, 124.93) * mm, "mid": v(144.46, 124.44) * mm, "end": v(144.56, 123.3) * mm});
            skPoint(sketch, "E302.visualSharp", {"position": v(217.32, 125.47) * mm});
            skArc(sketch, "E302.filletArc", {"start": v(215.44, 123.3) * mm, "mid": v(215.54, 124.44) * mm, "end": v(214.5, 124.93) * mm});
            skPoint(sketch, "E303.visualSharp", {"position": v(191.09, 19.2) * mm});
            skArc(sketch, "E303.filletArc", {"start": v(191.37, 21.54) * mm, "mid": v(191.86, 20.55) * mm, "end": v(192.97, 20.62) * mm});
            skPoint(sketch, "E304.visualSharp", {"position": v(258.91, 136.68) * mm});
            skArc(sketch, "E304.filletArc", {"start": v(258.63, 134.35) * mm, "mid": v(258.14, 135.34) * mm, "end": v(257.03, 135.27) * mm});
            skPoint(sketch, "E305.visualSharp", {"position": v(232.68, 30.41) * mm});
            skArc(sketch, "E305.filletArc", {"start": v(234.56, 32.6) * mm, "mid": v(234.46, 31.44) * mm, "end": v(235.5, 30.96) * mm});
            skPoint(sketch, "E306.visualSharp", {"position": v(279.16, 138.08) * mm});
            skArc(sketch, "E306.filletArc", {"start": v(280.58, 137.05) * mm, "mid": v(279.58, 137.16) * mm, "end": v(279, 136.35) * mm});
            skPoint(sketch, "E307.visualSharp", {"position": v(349.16, 16.84) * mm});
            skArc(sketch, "E307.filletArc", {"start": v(347.58, 17.56) * mm, "mid": v(348.58, 17.66) * mm, "end": v(348.98, 18.58) * mm});
            skPoint(sketch, "E308.visualSharp", {"position": v(-247.82, 155.88) * mm});
            skArc(sketch, "E308.filletArc", {"start": v(-245.66, 156.8) * mm, "mid": v(-246.28, 155.88) * mm, "end": v(-245.66, 154.96) * mm});
            skPoint(sketch, "E309.visualSharp", {"position": v(-112.18, 155.88) * mm});
            skArc(sketch, "E309.filletArc", {"start": v(-114.34, 154.96) * mm, "mid": v(-113.72, 155.88) * mm, "end": v(-114.34, 156.8) * mm});
            skPoint(sketch, "E310.visualSharp", {"position": v(-67.82, 155.88) * mm});
            skArc(sketch, "E310.filletArc", {"start": v(-65.66, 156.8) * mm, "mid": v(-66.28, 155.88) * mm, "end": v(-65.66, 154.96) * mm});
            skPoint(sketch, "E311.visualSharp", {"position": v(67.82, 155.88) * mm});
            skArc(sketch, "E311.filletArc", {"start": v(65.66, 154.96) * mm, "mid": v(66.28, 155.88) * mm, "end": v(65.66, 156.8) * mm});
            skPoint(sketch, "E312.visualSharp", {"position": v(112.18, 155.88) * mm});
            skArc(sketch, "E312.filletArc", {"start": v(114.34, 156.8) * mm, "mid": v(113.72, 155.88) * mm, "end": v(114.34, 154.96) * mm});
            skPoint(sketch, "E313.visualSharp", {"position": v(247.82, 155.88) * mm});
            skArc(sketch, "E313.filletArc", {"start": v(245.66, 154.96) * mm, "mid": v(246.28, 155.88) * mm, "end": v(245.66, 156.8) * mm});
            skPoint(sketch, "E314.visualSharp", {"position": v(142.68, 186.3) * mm});
            skArc(sketch, "E314.filletArc", {"start": v(144.56, 188.47) * mm, "mid": v(144.46, 187.33) * mm, "end": v(145.5, 186.84) * mm});
            skPoint(sketch, "E315.visualSharp", {"position": v(189.16, 293.97) * mm});
            skArc(sketch, "E315.filletArc", {"start": v(190.58, 292.94) * mm, "mid": v(189.58, 293.05) * mm, "end": v(189, 292.24) * mm});
            skPoint(sketch, "E316.visualSharp", {"position": v(259.16, 172.72) * mm});
            skArc(sketch, "E316.filletArc", {"start": v(257.58, 173.44) * mm, "mid": v(258.58, 173.54) * mm, "end": v(258.98, 174.46) * mm});
            skPoint(sketch, "E317.visualSharp", {"position": v(-259.16, 172.72) * mm});
            skArc(sketch, "E317.filletArc", {"start": v(-258.98, 174.46) * mm, "mid": v(-258.58, 173.54) * mm, "end": v(-257.58, 173.44) * mm});
            skPoint(sketch, "E318.visualSharp", {"position": v(-142.68, 186.3) * mm});
            skArc(sketch, "E318.filletArc", {"start": v(-145.5, 186.84) * mm, "mid": v(-144.46, 187.33) * mm, "end": v(-144.56, 188.47) * mm});
            skPoint(sketch, "E319.visualSharp", {"position": v(-189.16, 293.97) * mm});
            skArc(sketch, "E319.filletArc", {"start": v(-189, 292.24) * mm, "mid": v(-189.58, 293.05) * mm, "end": v(-190.58, 292.94) * mm});
            skPoint(sketch, "E320.visualSharp", {"position": v(-168.91, 292.56) * mm});
            skArc(sketch, "E320.filletArc", {"start": v(-167.03, 291.15) * mm, "mid": v(-168.14, 291.22) * mm, "end": v(-168.63, 290.23) * mm});
            skPoint(sketch, "E321.visualSharp", {"position": v(-101.09, 175.1) * mm});
            skArc(sketch, "E321.filletArc", {"start": v(-102.97, 176.5) * mm, "mid": v(-101.86, 176.43) * mm, "end": v(-101.37, 177.42) * mm});
            skPoint(sketch, "E322.visualSharp", {"position": v(101.09, 175.1) * mm});
            skArc(sketch, "E322.filletArc", {"start": v(101.37, 177.42) * mm, "mid": v(101.86, 176.43) * mm, "end": v(102.97, 176.5) * mm});
            skPoint(sketch, "E323.visualSharp", {"position": v(168.91, 292.56) * mm});
            skArc(sketch, "E323.filletArc", {"start": v(168.63, 290.23) * mm, "mid": v(168.14, 291.22) * mm, "end": v(167.03, 291.15) * mm});
            skPoint(sketch, "E324.visualSharp", {"position": v(-37.32, 186.3) * mm});
            skArc(sketch, "E324.filletArc", {"start": v(-35.44, 188.47) * mm, "mid": v(-35.54, 187.33) * mm, "end": v(-34.5, 186.84) * mm});
            skPoint(sketch, "E325.visualSharp", {"position": v(0, 250.94) * mm});
            skArc(sketch, "E325.filletArc", {"start": v(0.94, 248.22) * mm, "mid": v(0, 248.89) * mm, "end": v(-0.94, 248.22) * mm});
            skPoint(sketch, "E326.visualSharp", {"position": v(37.32, 186.3) * mm});
            skArc(sketch, "E326.filletArc", {"start": v(34.5, 186.84) * mm, "mid": v(35.54, 187.33) * mm, "end": v(35.44, 188.47) * mm});
            skPoint(sketch, "E327.visualSharp", {"position": v(-11.09, 292.56) * mm});
            skArc(sketch, "E327.filletArc", {"start": v(-11.37, 290.23) * mm, "mid": v(-11.86, 291.22) * mm, "end": v(-12.97, 291.15) * mm});
            skPoint(sketch, "E328.visualSharp", {"position": v(-78.91, 175.1) * mm});
            skArc(sketch, "E328.filletArc", {"start": v(-78.63, 177.42) * mm, "mid": v(-78.14, 176.43) * mm, "end": v(-77.03, 176.5) * mm});
            skPoint(sketch, "E329.visualSharp", {"position": v(11.09, 292.56) * mm});
            skArc(sketch, "E329.filletArc", {"start": v(12.97, 291.15) * mm, "mid": v(11.86, 291.22) * mm, "end": v(11.37, 290.23) * mm});
            skPoint(sketch, "E330.visualSharp", {"position": v(78.91, 175.1) * mm});
            skArc(sketch, "E330.filletArc", {"start": v(77.03, 176.5) * mm, "mid": v(78.14, 176.43) * mm, "end": v(78.63, 177.42) * mm});
            skPoint(sketch, "E331.visualSharp", {"position": v(90, 216.71) * mm});
            skArc(sketch, "E331.filletArc", {"start": v(89.06, 219.43) * mm, "mid": v(90, 218.77) * mm, "end": v(90.94, 219.43) * mm});
            skPoint(sketch, "E332.visualSharp", {"position": v(20, 310.8) * mm});
            skArc(sketch, "E332.filletArc", {"start": v(21.6, 311.52) * mm, "mid": v(21, 310.7) * mm, "end": v(21.41, 309.8) * mm});
            skPoint(sketch, "E333.visualSharp", {"position": v(160, 310.8) * mm});
            skArc(sketch, "E333.filletArc", {"start": v(158.59, 309.8) * mm, "mid": v(159, 310.7) * mm, "end": v(158.4, 311.52) * mm});
            skPoint(sketch, "E334.visualSharp", {"position": v(-160, 310.8) * mm});
            skArc(sketch, "E334.filletArc", {"start": v(-158.4, 311.52) * mm, "mid": v(-159, 310.7) * mm, "end": v(-158.59, 309.8) * mm});
            skPoint(sketch, "E335.visualSharp", {"position": v(-90, 216.71) * mm});
            skArc(sketch, "E335.filletArc", {"start": v(-90.94, 219.43) * mm, "mid": v(-90, 218.77) * mm, "end": v(-89.06, 219.43) * mm});
            skPoint(sketch, "E336.visualSharp", {"position": v(-20, 310.8) * mm});
            skArc(sketch, "E336.filletArc", {"start": v(-21.41, 309.8) * mm, "mid": v(-21, 310.7) * mm, "end": v(-21.6, 311.52) * mm});
            skSolve(sketch);
        }
        {
            var Q0;
            Q0=makeQuery(id+"F0.imprint","IMPRINT",FACE,{"disambiguationData":[TD([[makeQuery(id+"F0.imprint","IMPRINT",EDGE,{"derivedFrom":sQuery(id+"F0.wireOp",EDGE,"E0")}),-1.0]])]});
            extrude(context, id + "F1", {"entities" : qUnion([Q0]), "depth" : 3 * mm});
        }
        {
            var Q0;
            Q0=makeQuery(id+"F1.opExtrude","CAP_FACE",FACE,{"disambiguationData":[OSD([sQuery(id+"F0.wireOp",EDGE,"E0"),sQuery(id+"F0.wireOp",EDGE,"E1"),sQuery(id+"F0.wireOp",EDGE,"E2"),sQuery(id+"F0.wireOp",EDGE,"E3"),sQuery(id+"F0.wireOp",EDGE,"E4"),sQuery(id+"F0.wireOp",EDGE,"E5"),sQuery(id+"F0.wireOp",EDGE,"E6"),sQuery(id+"F0.wireOp",EDGE,"E7"),sQuery(id+"F0.wireOp",EDGE,"E8"),sQuery(id+"F0.wireOp",EDGE,"E9"),sQuery(id+"F0.wireOp",EDGE,"E10"),sQuery(id+"F0.wireOp",EDGE,"E11"),sQuery(id+"F0.wireOp",EDGE,"E12"),sQuery(id+"F0.wireOp",EDGE,"E13"),sQuery(id+"F0.wireOp",EDGE,"E14"),sQuery(id+"F0.wireOp",EDGE,"E15"),sQuery(id+"F0.wireOp",EDGE,"E16.trimOffspring"),sQuery(id+"F0.wireOp",EDGE,"E17.trimOffspring"),sQuery(id+"F0.wireOp",EDGE,"E18.trimOffspring"),sQuery(id+"F0.wireOp",EDGE,"E19.trimOffspring"),sQuery(id+"F0.wireOp",EDGE,"E20.trimOffspring"),sQuery(id+"F0.wireOp",EDGE,"E21.trimOffspring"),sQuery(id+"F0.wireOp",EDGE,"E22.trimOffspring"),sQuery(id+"F0.wireOp",EDGE,"E23.trimOffspring"),sQuery(id+"F0.wireOp",EDGE,"E24.trimOffspring"),sQuery(id+"F0.wireOp",EDGE,"E25.trimOffspring"),sQuery(id+"F0.wireOp",EDGE,"E26.trimOffspring"),sQuery(id+"F0.wireOp",EDGE,"E27.trimOffspring"),sQuery(id+"F0.wireOp",EDGE,"E28.trimOffspring"),sQuery(id+"F0.wireOp",EDGE,"E29.trimOffspring"),sQuery(id+"F0.wireOp",EDGE,"E30.trimOffspring"),sQuery(id+"F0.wireOp",EDGE,"E31.trimOffspring"),sQuery(id+"F0.wireOp",EDGE,"E32.trimOffspring"),sQuery(id+"F0.wireOp",EDGE,"E33.trimOffspring"),sQuery(id+"F0.wireOp",EDGE,"E34.trimOffspring"),sQuery(id+"F0.wireOp",EDGE,"E35.trimOffspring"),sQuery(id+"F0.wireOp",EDGE,"E36.trimOffspring"),sQuery(id+"F0.wireOp",EDGE,"E37.trimOffspring"),sQuery(id+"F0.wireOp",EDGE,"E38.trimOffspring"),sQuery(id+"F0.wireOp",EDGE,"E39.trimOffspring"),sQuery(id+"F0.wireOp",EDGE,"E40.trimOffspring"),sQuery(id+"F0.wireOp",EDGE,"E41.trimOffspring"),sQuery(id+"F0.wireOp",EDGE,"E42.trimOffspring"),sQuery(id+"F0.wireOp",EDGE,"E43.trimOffspring"),sQuery(id+"F0.wireOp",EDGE,"E44.trimOffspring"),sQuery(id+"F0.wireOp",EDGE,"E45.trimOffspring"),sQuery(id+"F0.wireOp",EDGE,"E46.trimOffspring"),sQuery(id+"F0.wireOp",EDGE,"E47.trimOffspring"),sQuery(id+"F0.wireOp",EDGE,"E48.trimOffspring"),sQuery(id+"F0.wireOp",EDGE,"E49.trimOffspring"),sQuery(id+"F0.wireOp",EDGE,"E50.trimOffspring"),sQuery(id+"F0.wireOp",EDGE,"E51.trimOffspring"),sQuery(id+"F0.wireOp",EDGE,"E52.trimOffspring"),sQuery(id+"F0.wireOp",EDGE,"E53.trimOffspring"),sQuery(id+"F0.wireOp",EDGE,"E54.trimOffspring"),sQuery(id+"F0.wireOp",EDGE,"E55.trimOffspring"),sQuery(id+"F0.wireOp",EDGE,"E56.trimOffspring"),sQuery(id+"F0.wireOp",EDGE,"E57.trimOffspring"),sQuery(id+"F0.wireOp",EDGE,"E58.trimOffspring"),sQuery(id+"F0.wireOp",EDGE,"E59.trimOffspring"),sQuery(id+"F0.wireOp",EDGE,"E60.trimOffspring"),sQuery(id+"F0.wireOp",EDGE,"E61.trimOffspring"),sQuery(id+"F0.wireOp",EDGE,"E62.trimOffspring"),sQuery(id+"F0.wireOp",EDGE,"E63.trimOffspring"),sQuery(id+"F0.wireOp",EDGE,"E64.trimOffspring"),sQuery(id+"F0.wireOp",EDGE,"E65.trimOffspring"),sQuery(id+"F0.wireOp",EDGE,"E66.trimOffspring"),sQuery(id+"F0.wireOp",EDGE,"E67.trimOffspring"),sQuery(id+"F0.wireOp",EDGE,"E68.trimOffspring"),sQuery(id+"F0.wireOp",EDGE,"E69.trimOffspring"),sQuery(id+"F0.wireOp",EDGE,"E70.trimOffspring"),sQuery(id+"F0.wireOp",EDGE,"E71.trimOffspring"),sQuery(id+"F0.wireOp",EDGE,"E72.trimOffspring"),sQuery(id+"F0.wireOp",EDGE,"E73.trimOffspring"),sQuery(id+"F0.wireOp",EDGE,"E74.trimOffspring"),sQuery(id+"F0.wireOp",EDGE,"E75.trimOffspring"),sQuery(id+"F0.wireOp",EDGE,"E76.trimOffspring"),sQuery(id+"F0.wireOp",EDGE,"E77.trimOffspring"),sQuery(id+"F0.wireOp",EDGE,"E78.trimOffspring"),sQuery(id+"F0.wireOp",EDGE,"E79.trimOffspring"),sQuery(id+"F0.wireOp",EDGE,"E80.trimOffspring"),sQuery(id+"F0.wireOp",EDGE,"E81.trimOffspring"),sQuery(id+"F0.wireOp",EDGE,"E82.trimOffspring"),sQuery(id+"F0.wireOp",EDGE,"E83.trimOffspring"),sQuery(id+"F0.wireOp",EDGE,"E84.trimOffspring"),sQuery(id+"F0.wireOp",EDGE,"E85.trimOffspring"),sQuery(id+"F0.wireOp",EDGE,"E86.trimOffspring"),sQuery(id+"F0.wireOp",EDGE,"E87.trimOffspring"),sQuery(id+"F0.wireOp",EDGE,"E88.trimOffspring"),sQuery(id+"F0.wireOp",EDGE,"E89.trimOffspring"),sQuery(id+"F0.wireOp",EDGE,"E90.trimOffspring"),sQuery(id+"F0.wireOp",EDGE,"E91.trimOffspring"),sQuery(id+"F0.wireOp",EDGE,"E92.trimOffspring"),sQuery(id+"F0.wireOp",EDGE,"E93.trimOffspring"),sQuery(id+"F0.wireOp",EDGE,"E94.trimOffspring"),sQuery(id+"F0.wireOp",EDGE,"E95.trimOffspring"),sQuery(id+"F0.wireOp",EDGE,"E96.trimOffspring"),sQuery(id+"F0.wireOp",EDGE,"E97.trimOffspring"),sQuery(id+"F0.wireOp",EDGE,"E98.trimOffspring"),sQuery(id+"F0.wireOp",EDGE,"E99.trimOffspring"),sQuery(id+"F0.wireOp",EDGE,"E100.trimOffspring"),sQuery(id+"F0.wireOp",EDGE,"E101.trimOffspring"),sQuery(id+"F0.wireOp",EDGE,"E102.trimOffspring"),sQuery(id+"F0.wireOp",EDGE,"E103.trimOffspring"),sQuery(id+"F0.wireOp",EDGE,"E104.trimOffspring"),sQuery(id+"F0.wireOp",EDGE,"E105.trimOffspring"),sQuery(id+"F0.wireOp",EDGE,"E106.trimOffspring"),sQuery(id+"F0.wireOp",EDGE,"E107.trimOffspring"),sQuery(id+"F0.wireOp",EDGE,"E108.trimOffspring"),sQuery(id+"F0.wireOp",EDGE,"E109.trimOffspring"),sQuery(id+"F0.wireOp",EDGE,"E110.trimOffspring"),sQuery(id+"F0.wireOp",EDGE,"E111.trimOffspring"),sQuery(id+"F0.wireOp",EDGE,"E112.trimOffspring"),sQuery(id+"F0.wireOp",EDGE,"E113.trimOffspring"),sQuery(id+"F0.wireOp",EDGE,"E114.trimOffspring"),sQuery(id+"F0.wireOp",EDGE,"E115.trimOffspring"),sQuery(id+"F0.wireOp",EDGE,"E116.trimOffspring"),sQuery(id+"F0.wireOp",EDGE,"E117.trimOffspring"),sQuery(id+"F0.wireOp",EDGE,"E118.trimOffspring"),sQuery(id+"F0.wireOp",EDGE,"E119.trimOffspring"),sQuery(id+"F0.wireOp",EDGE,"E120.trimOffspring"),sQuery(id+"F0.wireOp",EDGE,"E121.trimOffspring"),sQuery(id+"F0.wireOp",EDGE,"E122.trimOffspring"),sQuery(id+"F0.wireOp",EDGE,"E123.trimOffspring"),sQuery(id+"F0.wireOp",EDGE,"E124.trimOffspring"),sQuery(id+"F0.wireOp",EDGE,"E125.trimOffspring"),sQuery(id+"F0.wireOp",EDGE,"E126.trimOffspring"),sQuery(id+"F0.wireOp",EDGE,"E127.trimOffspring"),sQuery(id+"F0.wireOp",EDGE,"E128.trimOffspring"),sQuery(id+"F0.wireOp",EDGE,"E129.trimOffspring"),sQuery(id+"F0.wireOp",EDGE,"E130.trimOffspring"),sQuery(id+"F0.wireOp",EDGE,"E131.trimOffspring"),sQuery(id+"F0.wireOp",EDGE,"E132.trimOffspring"),sQuery(id+"F0.wireOp",EDGE,"E133.trimOffspring"),sQuery(id+"F0.wireOp",EDGE,"E134.trimOffspring"),sQuery(id+"F0.wireOp",EDGE,"E135.trimOffspring"),sQuery(id+"F0.wireOp",EDGE,"E136.trimOffspring"),sQuery(id+"F0.wireOp",EDGE,"E137.trimOffspring"),sQuery(id+"F0.wireOp",EDGE,"E138.trimOffspring"),sQuery(id+"F0.wireOp",EDGE,"E139.trimOffspring"),sQuery(id+"F0.wireOp",EDGE,"E140.trimOffspring"),sQuery(id+"F0.wireOp",EDGE,"E141.trimOffspring"),sQuery(id+"F0.wireOp",EDGE,"E142.trimOffspring"),sQuery(id+"F0.wireOp",EDGE,"E143.trimOffspring"),sQuery(id+"F0.wireOp",EDGE,"E144.trimOffspring"),sQuery(id+"F0.wireOp",EDGE,"E145.trimOffspring"),sQuery(id+"F0.wireOp",EDGE,"E146.trimOffspring"),sQuery(id+"F0.wireOp",EDGE,"E147.trimOffspring"),sQuery(id+"F0.wireOp",EDGE,"E148.trimOffspring"),sQuery(id+"F0.wireOp",EDGE,"E149.trimOffspring"),sQuery(id+"F0.wireOp",EDGE,"E150.trimOffspring"),sQuery(id+"F0.wireOp",EDGE,"E151.trimOffspring"),sQuery(id+"F0.wireOp",EDGE,"E152.trimOffspring"),sQuery(id+"F0.wireOp",EDGE,"E153.trimOffspring"),sQuery(id+"F0.wireOp",EDGE,"E154.trimOffspring"),sQuery(id+"F0.wireOp",EDGE,"E155.trimOffspring"),sQuery(id+"F0.wireOp",EDGE,"E156.trimOffspring"),sQuery(id+"F0.wireOp",EDGE,"E157.trimOffspring"),sQuery(id+"F0.wireOp",EDGE,"E158.trimOffspring"),sQuery(id+"F0.wireOp",EDGE,"E159.trimOffspring"),sQuery(id+"F0.wireOp",EDGE,"E160.trimOffspring"),sQuery(id+"F0.wireOp",EDGE,"E161.trimOffspring"),sQuery(id+"F0.wireOp",EDGE,"E162.trimOffspring"),sQuery(id+"F0.wireOp",EDGE,"E163.trimOffspring"),sQuery(id+"F0.wireOp",EDGE,"E164.trimOffspring"),sQuery(id+"F0.wireOp",EDGE,"E165.trimOffspring"),sQuery(id+"F0.wireOp",EDGE,"E166.trimOffspring"),sQuery(id+"F0.wireOp",EDGE,"E167.trimOffspring"),sQuery(id+"F0.wireOp",EDGE,"E168.trimOffspring"),sQuery(id+"F0.wireOp",EDGE,"E169.filletArc"),sQuery(id+"F0.wireOp",EDGE,"E170.filletArc"),sQuery(id+"F0.wireOp",EDGE,"E171.filletArc"),sQuery(id+"F0.wireOp",EDGE,"E172.filletArc"),sQuery(id+"F0.wireOp",EDGE,"E173.filletArc"),sQuery(id+"F0.wireOp",EDGE,"E174.filletArc"),sQuery(id+"F0.wireOp",EDGE,"E175.filletArc"),sQuery(id+"F0.wireOp",EDGE,"E176.filletArc"),sQuery(id+"F0.wireOp",EDGE,"E177.filletArc"),sQuery(id+"F0.wireOp",EDGE,"E178.filletArc"),sQuery(id+"F0.wireOp",EDGE,"E179.filletArc"),sQuery(id+"F0.wireOp",EDGE,"E180.filletArc"),sQuery(id+"F0.wireOp",EDGE,"E181.filletArc"),sQuery(id+"F0.wireOp",EDGE,"E182.filletArc"),sQuery(id+"F0.wireOp",EDGE,"E183.filletArc"),sQuery(id+"F0.wireOp",EDGE,"E184.filletArc"),sQuery(id+"F0.wireOp",EDGE,"E185.filletArc"),sQuery(id+"F0.wireOp",EDGE,"E186.filletArc"),sQuery(id+"F0.wireOp",EDGE,"E187.filletArc"),sQuery(id+"F0.wireOp",EDGE,"E188.filletArc"),sQuery(id+"F0.wireOp",EDGE,"E189.filletArc"),sQuery(id+"F0.wireOp",EDGE,"E190.filletArc"),sQuery(id+"F0.wireOp",EDGE,"E191.filletArc"),sQuery(id+"F0.wireOp",EDGE,"E192.filletArc"),sQuery(id+"F0.wireOp",EDGE,"E193.filletArc"),sQuery(id+"F0.wireOp",EDGE,"E194.filletArc"),sQuery(id+"F0.wireOp",EDGE,"E195.filletArc"),sQuery(id+"F0.wireOp",EDGE,"E196.filletArc"),sQuery(id+"F0.wireOp",EDGE,"E197.filletArc"),sQuery(id+"F0.wireOp",EDGE,"E198.filletArc"),sQuery(id+"F0.wireOp",EDGE,"E199.filletArc"),sQuery(id+"F0.wireOp",EDGE,"E200.filletArc"),sQuery(id+"F0.wireOp",EDGE,"E201.filletArc"),sQuery(id+"F0.wireOp",EDGE,"E202.filletArc"),sQuery(id+"F0.wireOp",EDGE,"E203.filletArc"),sQuery(id+"F0.wireOp",EDGE,"E204.filletArc"),sQuery(id+"F0.wireOp",EDGE,"E205.filletArc"),sQuery(id+"F0.wireOp",EDGE,"E206.filletArc"),sQuery(id+"F0.wireOp",EDGE,"E207.filletArc"),sQuery(id+"F0.wireOp",EDGE,"E208.filletArc"),sQuery(id+"F0.wireOp",EDGE,"E209.filletArc"),sQuery(id+"F0.wireOp",EDGE,"E210.filletArc"),sQuery(id+"F0.wireOp",EDGE,"E211.filletArc"),sQuery(id+"F0.wireOp",EDGE,"E212.filletArc"),sQuery(id+"F0.wireOp",EDGE,"E213.filletArc"),sQuery(id+"F0.wireOp",EDGE,"E214.filletArc"),sQuery(id+"F0.wireOp",EDGE,"E215.filletArc"),sQuery(id+"F0.wireOp",EDGE,"E216.filletArc"),sQuery(id+"F0.wireOp",EDGE,"E217.filletArc"),sQuery(id+"F0.wireOp",EDGE,"E218.filletArc"),sQuery(id+"F0.wireOp",EDGE,"E219.filletArc"),sQuery(id+"F0.wireOp",EDGE,"E220.filletArc"),sQuery(id+"F0.wireOp",EDGE,"E221.filletArc"),sQuery(id+"F0.wireOp",EDGE,"E222.filletArc"),sQuery(id+"F0.wireOp",EDGE,"E223.filletArc"),sQuery(id+"F0.wireOp",EDGE,"E224.filletArc"),sQuery(id+"F0.wireOp",EDGE,"E225.filletArc"),sQuery(id+"F0.wireOp",EDGE,"E226.filletArc"),sQuery(id+"F0.wireOp",EDGE,"E227.filletArc"),sQuery(id+"F0.wireOp",EDGE,"E228.filletArc"),sQuery(id+"F0.wireOp",EDGE,"E229.filletArc"),sQuery(id+"F0.wireOp",EDGE,"E230.filletArc"),sQuery(id+"F0.wireOp",EDGE,"E231.filletArc"),sQuery(id+"F0.wireOp",EDGE,"E232.filletArc"),sQuery(id+"F0.wireOp",EDGE,"E233.filletArc"),sQuery(id+"F0.wireOp",EDGE,"E234.filletArc"),sQuery(id+"F0.wireOp",EDGE,"E235.filletArc"),sQuery(id+"F0.wireOp",EDGE,"E236.filletArc"),sQuery(id+"F0.wireOp",EDGE,"E237.filletArc"),sQuery(id+"F0.wireOp",EDGE,"E238.filletArc"),sQuery(id+"F0.wireOp",EDGE,"E239.filletArc"),sQuery(id+"F0.wireOp",EDGE,"E240.filletArc"),sQuery(id+"F0.wireOp",EDGE,"E241.filletArc"),sQuery(id+"F0.wireOp",EDGE,"E242.filletArc"),sQuery(id+"F0.wireOp",EDGE,"E243.filletArc"),sQuery(id+"F0.wireOp",EDGE,"E244.filletArc"),sQuery(id+"F0.wireOp",EDGE,"E245.filletArc"),sQuery(id+"F0.wireOp",EDGE,"E246.filletArc"),sQuery(id+"F0.wireOp",EDGE,"E247.filletArc"),sQuery(id+"F0.wireOp",EDGE,"E248.filletArc"),sQuery(id+"F0.wireOp",EDGE,"E249.filletArc"),sQuery(id+"F0.wireOp",EDGE,"E250.filletArc"),sQuery(id+"F0.wireOp",EDGE,"E251.filletArc"),sQuery(id+"F0.wireOp",EDGE,"E252.filletArc"),sQuery(id+"F0.wireOp",EDGE,"E253.filletArc"),sQuery(id+"F0.wireOp",EDGE,"E254.filletArc"),sQuery(id+"F0.wireOp",EDGE,"E255.filletArc"),sQuery(id+"F0.wireOp",EDGE,"E256.filletArc"),sQuery(id+"F0.wireOp",EDGE,"E257.filletArc"),sQuery(id+"F0.wireOp",EDGE,"E258.filletArc"),sQuery(id+"F0.wireOp",EDGE,"E259.filletArc"),sQuery(id+"F0.wireOp",EDGE,"E260.filletArc"),sQuery(id+"F0.wireOp",EDGE,"E261.filletArc"),sQuery(id+"F0.wireOp",EDGE,"E262.filletArc"),sQuery(id+"F0.wireOp",EDGE,"E263.filletArc"),sQuery(id+"F0.wireOp",EDGE,"E264.filletArc"),sQuery(id+"F0.wireOp",EDGE,"E265.filletArc"),sQuery(id+"F0.wireOp",EDGE,"E266.filletArc"),sQuery(id+"F0.wireOp",EDGE,"E267.filletArc"),sQuery(id+"F0.wireOp",EDGE,"E268.filletArc"),sQuery(id+"F0.wireOp",EDGE,"E269.filletArc"),sQuery(id+"F0.wireOp",EDGE,"E270.filletArc"),sQuery(id+"F0.wireOp",EDGE,"E271.filletArc"),sQuery(id+"F0.wireOp",EDGE,"E272.filletArc"),sQuery(id+"F0.wireOp",EDGE,"E273.filletArc"),sQuery(id+"F0.wireOp",EDGE,"E274.filletArc"),sQuery(id+"F0.wireOp",EDGE,"E275.filletArc"),sQuery(id+"F0.wireOp",EDGE,"E276.filletArc"),sQuery(id+"F0.wireOp",EDGE,"E277.filletArc"),sQuery(id+"F0.wireOp",EDGE,"E278.filletArc"),sQuery(id+"F0.wireOp",EDGE,"E279.filletArc"),sQuery(id+"F0.wireOp",EDGE,"E280.filletArc"),sQuery(id+"F0.wireOp",EDGE,"E281.filletArc"),sQuery(id+"F0.wireOp",EDGE,"E282.filletArc"),sQuery(id+"F0.wireOp",EDGE,"E283.filletArc"),sQuery(id+"F0.wireOp",EDGE,"E284.filletArc"),sQuery(id+"F0.wireOp",EDGE,"E285.filletArc"),sQuery(id+"F0.wireOp",EDGE,"E286.filletArc"),sQuery(id+"F0.wireOp",EDGE,"E287.filletArc"),sQuery(id+"F0.wireOp",EDGE,"E288.filletArc"),sQuery(id+"F0.wireOp",EDGE,"E289.filletArc"),sQuery(id+"F0.wireOp",EDGE,"E290.filletArc"),sQuery(id+"F0.wireOp",EDGE,"E291.filletArc"),sQuery(id+"F0.wireOp",EDGE,"E292.filletArc"),sQuery(id+"F0.wireOp",EDGE,"E293.filletArc"),sQuery(id+"F0.wireOp",EDGE,"E294.filletArc"),sQuery(id+"F0.wireOp",EDGE,"E295.filletArc"),sQuery(id+"F0.wireOp",EDGE,"E296.filletArc"),sQuery(id+"F0.wireOp",EDGE,"E297.filletArc"),sQuery(id+"F0.wireOp",EDGE,"E298.filletArc"),sQuery(id+"F0.wireOp",EDGE,"E299.filletArc"),sQuery(id+"F0.wireOp",EDGE,"E300.filletArc"),sQuery(id+"F0.wireOp",EDGE,"E301.filletArc"),sQuery(id+"F0.wireOp",EDGE,"E302.filletArc"),sQuery(id+"F0.wireOp",EDGE,"E303.filletArc"),sQuery(id+"F0.wireOp",EDGE,"E304.filletArc"),sQuery(id+"F0.wireOp",EDGE,"E305.filletArc"),sQuery(id+"F0.wireOp",EDGE,"E306.filletArc"),sQuery(id+"F0.wireOp",EDGE,"E307.filletArc"),sQuery(id+"F0.wireOp",EDGE,"E308.filletArc"),sQuery(id+"F0.wireOp",EDGE,"E309.filletArc"),sQuery(id+"F0.wireOp",EDGE,"E310.filletArc"),sQuery(id+"F0.wireOp",EDGE,"E311.filletArc"),sQuery(id+"F0.wireOp",EDGE,"E312.filletArc"),sQuery(id+"F0.wireOp",EDGE,"E313.filletArc"),sQuery(id+"F0.wireOp",EDGE,"E314.filletArc"),sQuery(id+"F0.wireOp",EDGE,"E315.filletArc"),sQuery(id+"F0.wireOp",EDGE,"E316.filletArc"),sQuery(id+"F0.wireOp",EDGE,"E317.filletArc"),sQuery(id+"F0.wireOp",EDGE,"E318.filletArc"),sQuery(id+"F0.wireOp",EDGE,"E319.filletArc"),sQuery(id+"F0.wireOp",EDGE,"E320.filletArc"),sQuery(id+"F0.wireOp",EDGE,"E321.filletArc"),sQuery(id+"F0.wireOp",EDGE,"E322.filletArc"),sQuery(id+"F0.wireOp",EDGE,"E323.filletArc"),sQuery(id+"F0.wireOp",EDGE,"E324.filletArc"),sQuery(id+"F0.wireOp",EDGE,"E325.filletArc"),sQuery(id+"F0.wireOp",EDGE,"E326.filletArc"),sQuery(id+"F0.wireOp",EDGE,"E327.filletArc"),sQuery(id+"F0.wireOp",EDGE,"E328.filletArc"),sQuery(id+"F0.wireOp",EDGE,"E329.filletArc"),sQuery(id+"F0.wireOp",EDGE,"E330.filletArc"),sQuery(id+"F0.wireOp",EDGE,"E331.filletArc"),sQuery(id+"F0.wireOp",EDGE,"E332.filletArc"),sQuery(id+"F0.wireOp",EDGE,"E333.filletArc"),sQuery(id+"F0.wireOp",EDGE,"E334.filletArc"),sQuery(id+"F0.wireOp",EDGE,"E335.filletArc"),sQuery(id+"F0.wireOp",EDGE,"E336.filletArc")])],"isStart":false});
            var sketch = newSketch(context, id + "F2", { "sketchPlane" : qUnion([Q0])});
            skLineSegment(sketch, "E337", {"start": v(-268.47, 155) * mm, "end": v(0, 310) * mm, "construction": true});
            skLineSegment(sketch, "E338", {"start": v(0, 310) * mm, "end": v(268.47, 155) * mm, "construction": true});
            skLineSegment(sketch, "E339", {"start": v(268.47, 155) * mm, "end": v(268.47, -155) * mm, "construction": true});
            skLineSegment(sketch, "E340", {"start": v(268.47, -155) * mm, "end": v(0, -310) * mm, "construction": true});
            skLineSegment(sketch, "E341", {"start": v(0, -310) * mm, "end": v(-268.47, -155) * mm, "construction": true});
            skLineSegment(sketch, "E342", {"start": v(-268.47, -155) * mm, "end": v(-268.47, 155) * mm, "construction": true});
            skCircle(sketch, "E343", {"center": v(0, 310) * mm, "radius": 5 * mm});
            skCircle(sketch, "E344", {"center": v(268.47, -155) * mm, "radius": 5 * mm});
            skCircle(sketch, "E345", {"center": v(0, -310) * mm, "radius": 5 * mm});
            skCircle(sketch, "E346", {"center": v(-268.47, -155) * mm, "radius": 5 * mm});
            skCircle(sketch, "E347", {"center": v(-268.47, 155) * mm, "radius": 5 * mm});
            skCircle(sketch, "E348", {"center": v(268.47, 155) * mm, "radius": 5 * mm});
            skSolve(sketch);
        }
        {
            var Q0;
            Q0=makeQuery(id+"F2.imprint","IMPRINT",FACE,{"disambiguationData":[TD([[makeQuery(id+"F2.imprint","IMPRINT",EDGE,{"derivedFrom":sQuery(id+"F2.wireOp",EDGE,"E343")}),-1.0]])]});
            extrude(context, id + "F3", {"entities" : qUnion([Q0]), "operationType" : NewBodyOperationType.INTERSECT, "oppositeDirection" : true, "depth" : 5 * mm});
        }
    });
